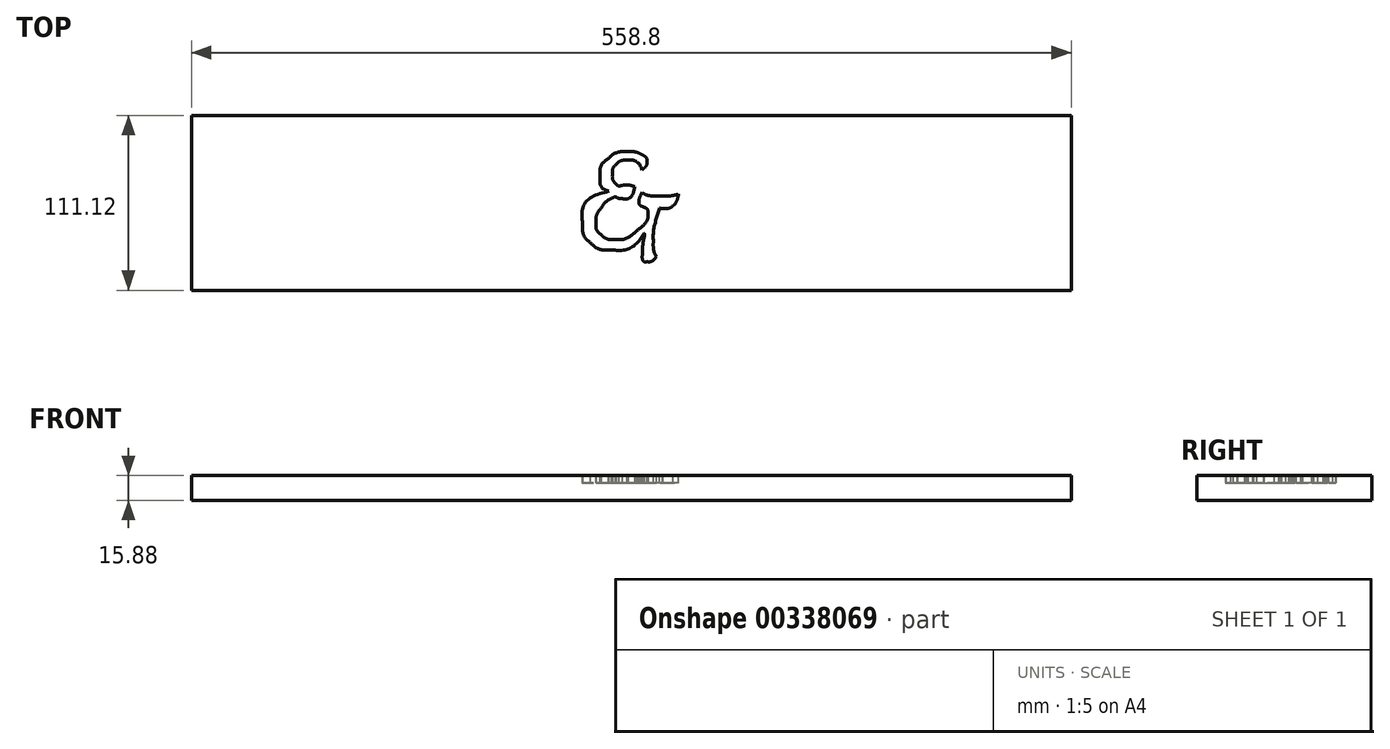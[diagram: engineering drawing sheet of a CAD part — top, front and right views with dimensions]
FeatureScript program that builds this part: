
annotation { "Feature Type Name" : "Feature", "Feature Type Description" : "" }
export const myFeature = defineFeature(function(context is Context, id is Id, definition is map)
    precondition{}
    {
        {
            var Q0;
            Q0=qCreatedBy(makeId("Top.planeOp"),FACE);
            var sketch = newSketch(context, id + "F0", { "sketchPlane" : qUnion([Q0])});
            skLineSegment(sketch, "E0.bottom", {"start": v(12.7, 0) * mm, "end": v(546.1, 0) * mm});
            skLineSegment(sketch, "E0.top", {"start": v(12.7, 609.6) * mm, "end": v(546.1, 609.6) * mm});
            skLineSegment(sketch, "E0.left", {"start": v(0, 12.7) * mm, "end": v(0, 596.9) * mm});
            skLineSegment(sketch, "E0.right", {"start": v(558.8, 12.7) * mm, "end": v(558.8, 596.9) * mm});
            skPoint(sketch, "E1.visualSharp", {"position": v(0, 609.6) * mm});
            skArc(sketch, "E1.filletArc", {"start": v(12.7, 609.6) * mm, "mid": v(3.72, 605.88) * mm, "end": v(0, 596.9) * mm});
            skPoint(sketch, "E2.visualSharp", {"position": v(0, 0) * mm});
            skArc(sketch, "E2.filletArc", {"start": v(0, 12.7) * mm, "mid": v(3.72, 3.72) * mm, "end": v(12.7, 0) * mm});
            skPoint(sketch, "E3.visualSharp", {"position": v(558.8, 0) * mm});
            skArc(sketch, "E3.filletArc", {"start": v(546.1, 0) * mm, "mid": v(555.08, 3.72) * mm, "end": v(558.8, 12.7) * mm});
            skPoint(sketch, "E4.visualSharp", {"position": v(558.8, 609.6) * mm});
            skArc(sketch, "E4.filletArc", {"start": v(558.8, 596.9) * mm, "mid": v(555.08, 605.88) * mm, "end": v(546.1, 609.6) * mm});
            skSolve(sketch);
        }
        {
            var Q0;
            Q0=makeQuery(id+"F0.imprint","IMPRINT",FACE,{"disambiguationData":[TD([[makeQuery(id+"F0.imprint","IMPRINT",EDGE,{"derivedFrom":sQuery(id+"F0.wireOp",EDGE,"E0.bottom")}),1.0]])]});
            extrude(context, id + "F1", {"entities" : qUnion([Q0]), "depth" : 15.88 * mm});
        }
        {
            var Q0;
            Q0=makeQuery(id+"F1.opExtrude","CAP_FACE",FACE,{"disambiguationData":[OSD([sQuery(id+"F0.wireOp",EDGE,"E0.bottom"),sQuery(id+"F0.wireOp",EDGE,"E0.top"),sQuery(id+"F0.wireOp",EDGE,"E0.left"),sQuery(id+"F0.wireOp",EDGE,"E0.right"),sQuery(id+"F0.wireOp",EDGE,"E1.filletArc"),sQuery(id+"F0.wireOp",EDGE,"E2.filletArc"),sQuery(id+"F0.wireOp",EDGE,"E3.filletArc"),sQuery(id+"F0.wireOp",EDGE,"E4.filletArc")])],"isStart":false});
            var sketch = newSketch(context, id + "F2", { "sketchPlane" : qUnion([Q0])});
            skFitSpline(sketch, "E5", {"points": [v(247.46, 485.02) * mm, v(244.22, 485.02) * mm, v(241.38, 482.73) * mm, v(238.94, 478.15) * mm]});
            skFitSpline(sketch, "E6", {"points": [v(238.94, 478.15) * mm, v(236.48, 473.56) * mm, v(235.26, 468.05) * mm, v(235.26, 461.6) * mm]});
            skFitSpline(sketch, "E7", {"points": [v(235.26, 461.6) * mm, v(235.26, 456.87) * mm, v(236.54, 454.5) * mm, v(239.12, 454.5) * mm]});
            skFitSpline(sketch, "E8", {"points": [v(239.12, 454.5) * mm, v(242.2, 454.5) * mm, v(248.34, 462.57) * mm, v(257.6, 478.7) * mm]});
            skFitSpline(sketch, "E9", {"points": [v(257.6, 478.7) * mm, v(257.73, 478.94) * mm, v(258.18, 479.46) * mm, v(258.91, 480.26) * mm]});
            skFitSpline(sketch, "E10", {"points": [v(258.91, 480.26) * mm, v(254.36, 483.44) * mm, v(250.54, 485.02) * mm, v(247.46, 485.02) * mm]});
            skFitSpline(sketch, "E11", {"points": [v(371.38, 485.98) * mm, v(368.47, 485.98) * mm, v(365.74, 484.16) * mm, v(363.18, 480.52) * mm]});
            skFitSpline(sketch, "E12", {"points": [v(363.18, 480.52) * mm, v(360.62, 476.88) * mm, v(359.03, 472.72) * mm, v(358.4, 468.06) * mm]});
            skFitSpline(sketch, "E13", {"points": [v(358.4, 468.06) * mm, v(362.59, 468.32) * mm, v(366.35, 469.82) * mm, v(369.66, 472.53) * mm]});
            skFitSpline(sketch, "E14", {"points": [v(369.66, 472.53) * mm, v(372.98, 475.24) * mm, v(374.64, 478.32) * mm, v(374.64, 481.78) * mm]});
            skFitSpline(sketch, "E15", {"points": [v(374.64, 481.78) * mm, v(374.64, 484.58) * mm, v(373.55, 485.98) * mm, v(371.38, 485.98) * mm]});
            skFitSpline(sketch, "E16", {"points": [v(372.25, 491.45) * mm, v(375.43, 491.45) * mm, v(378, 490.53) * mm, v(379.95, 488.68) * mm]});
            skFitSpline(sketch, "E17", {"points": [v(379.95, 488.68) * mm, v(381.9, 486.84) * mm, v(382.89, 484.38) * mm, v(382.89, 481.3) * mm]});
            skFitSpline(sketch, "E18", {"points": [v(382.89, 481.3) * mm, v(382.89, 476.36) * mm, v(380.3, 472.02) * mm, v(375.12, 468.3) * mm]});
            skFitSpline(sketch, "E19", {"points": [v(375.12, 468.3) * mm, v(369.94, 464.57) * mm, v(364.27, 462.7) * mm, v(358.12, 462.7) * mm]});
            skFitSpline(sketch, "E20", {"points": [v(358.12, 462.7) * mm, v(358.12, 456.15) * mm, v(360.76, 452.87) * mm, v(366.01, 452.87) * mm]});
            skFitSpline(sketch, "E21", {"points": [v(366.01, 452.87) * mm, v(370.84, 452.87) * mm, v(376.2, 455.49) * mm, v(382.13, 460.74) * mm]});
            skFitSpline(sketch, "E22", {"points": [v(382.13, 460.74) * mm, v(388.04, 465.98) * mm, v(393.52, 473.06) * mm, v(398.54, 481.95) * mm]});
            skFitSpline(sketch, "E23", {"points": [v(402.5, 479.62) * mm, v(397.84, 469.55) * mm, v(391.82, 461.33) * mm, v(384.42, 454.98) * mm]});
            skFitSpline(sketch, "E24", {"points": [v(384.42, 454.98) * mm, v(377.03, 448.62) * mm, v(369.98, 445.45) * mm, v(363.3, 445.45) * mm]});
            skFitSpline(sketch, "E25", {"points": [v(363.3, 445.45) * mm, v(358.9, 445.45) * mm, v(355.42, 447.05) * mm, v(352.87, 450.22) * mm]});
            skFitSpline(sketch, "E26", {"points": [v(352.87, 450.22) * mm, v(350.64, 453) * mm, v(349.4, 456.61) * mm, v(349.1, 461.08) * mm]});
            skFitSpline(sketch, "E27", {"points": [v(349.1, 461.08) * mm, v(347.32, 458.56) * mm, v(345.51, 456.33) * mm, v(343.7, 454.35) * mm]});
            skFitSpline(sketch, "E28", {"points": [v(343.7, 454.35) * mm, v(338.24, 448.42) * mm, v(333.27, 445.45) * mm, v(328.8, 445.45) * mm]});
            skFitSpline(sketch, "E29", {"points": [v(328.8, 445.45) * mm, v(325.99, 445.45) * mm, v(323.71, 446.48) * mm, v(322, 448.54) * mm]});
            skFitSpline(sketch, "E30", {"points": [v(322, 448.54) * mm, v(320.27, 450.6) * mm, v(319.41, 453.3) * mm, v(319.41, 456.62) * mm]});
            skFitSpline(sketch, "E31", {"points": [v(319.41, 456.62) * mm, v(319.41, 457.85) * mm, v(319.64, 459.77) * mm, v(320.12, 462.36) * mm]});
            skLineSegment(sketch, "E32", {"start": v(398.54, 481.95) * mm, "end": v(402.5, 479.62) * mm});
            skLineSegment(sketch, "E33", {"start": v(402.5, 479.62) * mm, "end": v(398.54, 481.95) * mm});
            skFitSpline(sketch, "E34", {"points": [v(320.89, 466.68) * mm, v(322, 472.85) * mm, v(322.57, 477.15) * mm, v(322.57, 479.6) * mm]});
            skFitSpline(sketch, "E35", {"points": [v(322.57, 479.6) * mm, v(322.57, 480.87) * mm, v(322.18, 482.24) * mm, v(321.4, 483.7) * mm]});
            skFitSpline(sketch, "E36", {"points": [v(321.4, 483.7) * mm, v(324.84, 484.7) * mm, v(326.97, 485.22) * mm, v(327.78, 485.22) * mm]});
            skFitSpline(sketch, "E37", {"points": [v(327.78, 485.22) * mm, v(329.99, 485.22) * mm, v(331.1, 483.6) * mm, v(331.1, 480.35) * mm]});
            skFitSpline(sketch, "E38", {"points": [v(331.1, 480.35) * mm, v(331.1, 478.32) * mm, v(330.76, 475.38) * mm, v(330.07, 471.54) * mm]});
            skLineSegment(sketch, "E39", {"start": v(320.12, 462.36) * mm, "end": v(320.89, 466.68) * mm});
            skLineSegment(sketch, "E40", {"start": v(320.89, 466.68) * mm, "end": v(320.12, 462.36) * mm});
            skFitSpline(sketch, "E41", {"points": [v(328.7, 463.92) * mm, v(328.05, 460.32) * mm, v(327.73, 458) * mm, v(327.73, 456.92) * mm]});
            skFitSpline(sketch, "E42", {"points": [v(327.73, 456.92) * mm, v(327.73, 454.22) * mm, v(328.7, 452.87) * mm, v(330.64, 452.87) * mm]});
            skFitSpline(sketch, "E43", {"points": [v(330.64, 452.87) * mm, v(333.34, 452.87) * mm, v(337.06, 455.56) * mm, v(341.8, 460.93) * mm]});
            skFitSpline(sketch, "E44", {"points": [v(341.8, 460.93) * mm, v(344.6, 464.12) * mm, v(347.4, 467.87) * mm, v(350.2, 472.2) * mm]});
            skFitSpline(sketch, "E45", {"points": [v(350.2, 472.2) * mm, v(351.28, 476.24) * mm, v(353.16, 479.88) * mm, v(355.83, 483.14) * mm]});
            skFitSpline(sketch, "E46", {"points": [v(355.83, 483.14) * mm, v(360.35, 488.68) * mm, v(365.83, 491.45) * mm, v(372.25, 491.45) * mm]});
            skLineSegment(sketch, "E47", {"start": v(330.07, 471.54) * mm, "end": v(328.7, 463.92) * mm});
            skLineSegment(sketch, "E48", {"start": v(328.7, 463.92) * mm, "end": v(330.07, 471.54) * mm});
            skFitSpline(sketch, "E49", {"points": [v(305.1, 507.84) * mm, v(305.33, 507.84) * mm, v(306.14, 507.78) * mm, v(307.5, 507.65) * mm]});
            skFitSpline(sketch, "E50", {"points": [v(307.5, 507.65) * mm, v(305.64, 504.33) * mm, v(303.76, 499.96) * mm, v(301.86, 494.56) * mm]});
            skFitSpline(sketch, "E51", {"points": [v(319.5, 494.56) * mm, v(322.22, 494.56) * mm, v(324.64, 494.92) * mm, v(326.74, 495.67) * mm]});
            skFitSpline(sketch, "E52", {"points": [v(326.74, 495.67) * mm, v(326.87, 497.05) * mm, v(327.2, 498.41) * mm, v(327.69, 499.77) * mm]});
            skLineSegment(sketch, "E53", {"start": v(301.86, 494.56) * mm, "end": v(319.5, 494.56) * mm});
            skLineSegment(sketch, "E54", {"start": v(319.5, 494.56) * mm, "end": v(301.86, 494.56) * mm});
            skFitSpline(sketch, "E55", {"points": [v(328.67, 499.72) * mm, v(330.08, 499.79) * mm, v(332.2, 500.64) * mm, v(335.04, 502.28) * mm]});
            skFitSpline(sketch, "E56", {"points": [v(335.04, 502.28) * mm, v(337.9, 503.93) * mm, v(340.52, 505.68) * mm, v(342.94, 507.52) * mm]});
            skFitSpline(sketch, "E57", {"points": [v(342.94, 507.52) * mm, v(341.85, 503.08) * mm, v(340.03, 500.06) * mm, v(337.5, 498.48) * mm]});
            skFitSpline(sketch, "E58", {"points": [v(337.5, 498.48) * mm, v(333.26, 493.7) * mm, v(330.34, 491.32) * mm, v(328.76, 491.32) * mm]});
            skFitSpline(sketch, "E59", {"points": [v(328.76, 491.32) * mm, v(327.76, 491.32) * mm, v(327.1, 491.79) * mm, v(326.85, 492.72) * mm]});
            skFitSpline(sketch, "E60", {"points": [v(326.85, 492.72) * mm, v(326.33, 491.05) * mm, v(325.73, 489.92) * mm, v(325.02, 489.33) * mm]});
            skFitSpline(sketch, "E61", {"points": [v(325.02, 489.33) * mm, v(323.92, 488.4) * mm, v(321.98, 487.93) * mm, v(319.18, 487.93) * mm]});
            skLineSegment(sketch, "E62", {"start": v(327.69, 499.77) * mm, "end": v(328.67, 499.72) * mm});
            skLineSegment(sketch, "E63", {"start": v(328.67, 499.72) * mm, "end": v(327.69, 499.77) * mm});
            skFitSpline(sketch, "E64", {"points": [v(300.17, 487.93) * mm, v(300.04, 487.44) * mm, v(299.9, 486.92) * mm, v(299.75, 486.38) * mm]});
            skFitSpline(sketch, "E65", {"points": [v(299.75, 486.38) * mm, v(296.99, 475.84) * mm, v(295.6, 467.88) * mm, v(295.6, 462.47) * mm]});
            skFitSpline(sketch, "E66", {"points": [v(295.6, 462.47) * mm, v(295.6, 456.94) * mm, v(297.3, 454.18) * mm, v(300.68, 454.18) * mm]});
            skFitSpline(sketch, "E67", {"points": [v(300.68, 454.18) * mm, v(302.53, 454.18) * mm, v(304.57, 455.1) * mm, v(306.8, 456.9) * mm]});
            skFitSpline(sketch, "E68", {"points": [v(306.8, 456.9) * mm, v(309.05, 458.71) * mm, v(310.85, 460.91) * mm, v(312.2, 463.5) * mm]});
            skFitSpline(sketch, "E69", {"points": [v(312.2, 463.5) * mm, v(313.35, 461.8) * mm, v(313.92, 460.42) * mm, v(313.92, 459.33) * mm]});
            skFitSpline(sketch, "E70", {"points": [v(313.92, 459.33) * mm, v(313.92, 456.5) * mm, v(311.92, 453.5) * mm, v(307.92, 450.28) * mm]});
            skFitSpline(sketch, "E71", {"points": [v(307.92, 450.28) * mm, v(303.9, 447.06) * mm, v(300.24, 445.45) * mm, v(296.9, 445.45) * mm]});
            skFitSpline(sketch, "E72", {"points": [v(296.9, 445.45) * mm, v(293.88, 445.45) * mm, v(291.42, 446.93) * mm, v(289.56, 449.9) * mm]});
            skFitSpline(sketch, "E73", {"points": [v(289.56, 449.9) * mm, v(287.7, 452.87) * mm, v(286.76, 456.65) * mm, v(286.76, 461.23) * mm]});
            skFitSpline(sketch, "E74", {"points": [v(286.76, 461.23) * mm, v(286.76, 462.58) * mm, v(286.84, 464.08) * mm, v(287.02, 465.75) * mm]});
            skFitSpline(sketch, "E75", {"points": [v(287.02, 465.75) * mm, v(284.81, 462.56) * mm, v(282.47, 459.69) * mm, v(280.01, 457.13) * mm]});
            skFitSpline(sketch, "E76", {"points": [v(280.01, 457.13) * mm, v(274.37, 451.28) * mm, v(269.48, 448.36) * mm, v(265.31, 448.36) * mm]});
            skFitSpline(sketch, "E77", {"points": [v(265.31, 448.36) * mm, v(259.81, 448.36) * mm, v(257.07, 453.3) * mm, v(257.07, 463.23) * mm]});
            skFitSpline(sketch, "E78", {"points": [v(257.07, 463.23) * mm, v(257.07, 465.2) * mm, v(257.14, 467.57) * mm, v(257.28, 470.32) * mm]});
            skFitSpline(sketch, "E79", {"points": [v(257.28, 470.32) * mm, v(255.19, 463.64) * mm, v(251.91, 457.83) * mm, v(247.46, 452.87) * mm]});
            skFitSpline(sketch, "E80", {"points": [v(247.46, 452.87) * mm, v(242.99, 447.92) * mm, v(239.04, 445.45) * mm, v(235.6, 445.45) * mm]});
            skFitSpline(sketch, "E81", {"points": [v(235.6, 445.45) * mm, v(232.88, 445.45) * mm, v(230.72, 446.77) * mm, v(229.15, 449.4) * mm]});
            skFitSpline(sketch, "E82", {"points": [v(229.15, 449.4) * mm, v(227.56, 452.05) * mm, v(226.77, 455.51) * mm, v(226.77, 459.78) * mm]});
            skFitSpline(sketch, "E83", {"points": [v(226.77, 459.78) * mm, v(226.77, 468.13) * mm, v(229.03, 475.5) * mm, v(233.56, 481.87) * mm]});
            skFitSpline(sketch, "E84", {"points": [v(233.56, 481.87) * mm, v(238.09, 488.26) * mm, v(243.35, 491.45) * mm, v(249.38, 491.45) * mm]});
            skFitSpline(sketch, "E85", {"points": [v(249.38, 491.45) * mm, v(253.01, 491.45) * mm, v(256.66, 490.21) * mm, v(260.33, 487.76) * mm]});
            skFitSpline(sketch, "E86", {"points": [v(260.33, 487.76) * mm, v(260.86, 490.19) * mm, v(263.48, 491.4) * mm, v(268.16, 491.4) * mm]});
            skFitSpline(sketch, "E87", {"points": [v(268.16, 491.4) * mm, v(268.26, 491.4) * mm, v(268.96, 491.37) * mm, v(270.27, 491.3) * mm]});
            skFitSpline(sketch, "E88", {"points": [v(270.27, 491.3) * mm, v(268.9, 488.33) * mm, v(267.89, 484.93) * mm, v(267.2, 481.1) * mm]});
            skLineSegment(sketch, "E89", {"start": v(319.18, 487.93) * mm, "end": v(300.17, 487.93) * mm});
            skLineSegment(sketch, "E90", {"start": v(300.17, 487.93) * mm, "end": v(319.18, 487.93) * mm});
            skFitSpline(sketch, "E91", {"points": [v(266.62, 477.77) * mm, v(265.96, 474.15) * mm, v(265.63, 469.88) * mm, v(265.63, 464.94) * mm]});
            skFitSpline(sketch, "E92", {"points": [v(265.63, 464.94) * mm, v(265.63, 459.77) * mm, v(266.57, 457.18) * mm, v(268.44, 457.18) * mm]});
            skFitSpline(sketch, "E93", {"points": [v(268.44, 457.18) * mm, v(270.76, 457.18) * mm, v(274.05, 459.48) * mm, v(278.32, 464.1) * mm]});
            skFitSpline(sketch, "E94", {"points": [v(278.32, 464.1) * mm, v(281.96, 468.04) * mm, v(285.66, 473) * mm, v(289.42, 478.98) * mm]});
            skFitSpline(sketch, "E95", {"points": [v(289.42, 478.98) * mm, v(289.7, 480.18) * mm, v(290, 481.4) * mm, v(290.32, 482.69) * mm]});
            skLineSegment(sketch, "E96", {"start": v(267.2, 481.1) * mm, "end": v(266.62, 477.77) * mm});
            skLineSegment(sketch, "E97", {"start": v(266.62, 477.77) * mm, "end": v(267.2, 481.1) * mm});
            skFitSpline(sketch, "E98", {"points": [v(286.65, 487.93) * mm, v(284.3, 487.93) * mm, v(282.1, 487.54) * mm, v(280.04, 486.76) * mm]});
            skFitSpline(sketch, "E99", {"points": [v(280.04, 486.76) * mm, v(281.5, 490.38) * mm, v(282.72, 492.6) * mm, v(283.72, 493.38) * mm]});
            skFitSpline(sketch, "E100", {"points": [v(283.72, 493.38) * mm, v(284.71, 494.16) * mm, v(286.34, 494.56) * mm, v(288.6, 494.56) * mm]});
            skLineSegment(sketch, "E101", {"start": v(290.32, 482.69) * mm, "end": v(291.82, 487.93) * mm});
            skLineSegment(sketch, "E102", {"start": v(291.82, 487.93) * mm, "end": v(286.65, 487.93) * mm});
            skFitSpline(sketch, "E103", {"points": [v(293.99, 497.12) * mm, v(295.02, 501) * mm, v(296.33, 503.76) * mm, v(297.95, 505.4) * mm]});
            skFitSpline(sketch, "E104", {"points": [v(297.95, 505.4) * mm, v(299.55, 507.03) * mm, v(301.94, 507.84) * mm, v(305.1, 507.84) * mm]});
            skLineSegment(sketch, "E105", {"start": v(288.6, 494.56) * mm, "end": v(293.33, 494.56) * mm});
            skLineSegment(sketch, "E106", {"start": v(293.33, 494.56) * mm, "end": v(293.99, 497.12) * mm});
            skFitSpline(sketch, "E107", {"points": [v(178.41, 506.2) * mm, v(181.96, 506.2) * mm, v(186.85, 506.6) * mm, v(193.08, 507.4) * mm]});
            skFitSpline(sketch, "E108", {"points": [v(188.04, 478.85) * mm, v(200.42, 488.81) * mm, v(207.85, 498.44) * mm, v(210.33, 507.7) * mm]});
            skFitSpline(sketch, "E109", {"points": [v(210.33, 507.7) * mm, v(214.42, 505.56) * mm, v(216.46, 503.26) * mm, v(216.46, 500.79) * mm]});
            skFitSpline(sketch, "E110", {"points": [v(216.46, 500.79) * mm, v(216.46, 499.37) * mm, v(213.98, 496.13) * mm, v(209, 491.1) * mm]});
            skFitSpline(sketch, "E111", {"points": [v(209, 491.1) * mm, v(204.02, 486.08) * mm, v(199.1, 481.73) * mm, v(194.23, 478.07) * mm]});
            skFitSpline(sketch, "E112", {"points": [v(194.23, 478.07) * mm, v(198.39, 469.54) * mm, v(202.46, 462.52) * mm, v(206.43, 457.03) * mm]});
            skFitSpline(sketch, "E113", {"points": [v(206.43, 457.03) * mm, v(210.4, 451.54) * mm, v(213.38, 448.8) * mm, v(215.37, 448.8) * mm]});
            skFitSpline(sketch, "E114", {"points": [v(215.37, 448.8) * mm, v(217.55, 448.8) * mm, v(220.39, 450.27) * mm, v(223.87, 453.22) * mm]});
            skLineSegment(sketch, "E115", {"start": v(193.08, 507.4) * mm, "end": v(188.04, 478.85) * mm});
            skLineSegment(sketch, "E116", {"start": v(188.04, 478.85) * mm, "end": v(193.08, 507.4) * mm});
            skFitSpline(sketch, "E117", {"points": [v(223.98, 451.1) * mm, v(223.98, 449.09) * mm, v(222.68, 446.98) * mm, v(220.08, 444.73) * mm]});
            skFitSpline(sketch, "E118", {"points": [v(220.08, 444.73) * mm, v(217.49, 442.5) * mm, v(214.96, 441.38) * mm, v(212.51, 441.38) * mm]});
            skFitSpline(sketch, "E119", {"points": [v(212.51, 441.38) * mm, v(206.3, 441.38) * mm, v(197.85, 452.5) * mm, v(187.18, 474.76) * mm]});
            skLineSegment(sketch, "E120", {"start": v(223.87, 453.22) * mm, "end": v(223.98, 451.1) * mm});
            skLineSegment(sketch, "E121", {"start": v(223.98, 451.1) * mm, "end": v(223.87, 453.22) * mm});
            skFitSpline(sketch, "E122", {"points": [v(183.9, 454.8) * mm, v(183.48, 452.44) * mm, v(183.27, 450.88) * mm, v(183.27, 450.14) * mm]});
            skFitSpline(sketch, "E123", {"points": [v(183.27, 450.14) * mm, v(183.27, 449.5) * mm, v(183.42, 448.6) * mm, v(183.73, 447.42) * mm]});
            skFitSpline(sketch, "E124", {"points": [v(183.73, 447.42) * mm, v(180.96, 445.82) * mm, v(178.55, 445.01) * mm, v(176.52, 445.01) * mm]});
            skFitSpline(sketch, "E125", {"points": [v(176.52, 445.01) * mm, v(174.84, 445.01) * mm, v(174, 445.83) * mm, v(174, 447.45) * mm]});
            skFitSpline(sketch, "E126", {"points": [v(174, 447.45) * mm, v(174, 448.08) * mm, v(174.25, 449.8) * mm, v(174.74, 452.56) * mm]});
            skLineSegment(sketch, "E127", {"start": v(187.18, 474.76) * mm, "end": v(183.9, 454.8) * mm});
            skLineSegment(sketch, "E128", {"start": v(183.9, 454.8) * mm, "end": v(187.18, 474.76) * mm});
            skFitSpline(sketch, "E129", {"points": [v(183.17, 499.25) * mm, v(181.66, 498.94) * mm, v(180, 498.79) * mm, v(178.17, 498.79) * mm]});
            skFitSpline(sketch, "E130", {"points": [v(178.17, 498.79) * mm, v(174.1, 498.79) * mm, v(171.7, 502.02) * mm, v(170.94, 508.51) * mm]});
            skLineSegment(sketch, "E131", {"start": v(174.74, 452.56) * mm, "end": v(183.17, 499.25) * mm});
            skLineSegment(sketch, "E132", {"start": v(183.17, 499.25) * mm, "end": v(174.74, 452.56) * mm});
            skFitSpline(sketch, "E133", {"points": [v(247.46, 485.02) * mm, v(244.22, 485.02) * mm, v(241.38, 482.73) * mm, v(238.94, 478.15) * mm]});
            skFitSpline(sketch, "E134", {"points": [v(238.94, 478.15) * mm, v(236.48, 473.56) * mm, v(235.26, 468.05) * mm, v(235.26, 461.6) * mm]});
            skFitSpline(sketch, "E135", {"points": [v(235.26, 461.6) * mm, v(235.26, 456.87) * mm, v(236.54, 454.5) * mm, v(239.12, 454.5) * mm]});
            skFitSpline(sketch, "E136", {"points": [v(239.12, 454.5) * mm, v(242.2, 454.5) * mm, v(248.34, 462.57) * mm, v(257.6, 478.7) * mm]});
            skFitSpline(sketch, "E137", {"points": [v(257.6, 478.7) * mm, v(257.73, 478.94) * mm, v(258.18, 479.46) * mm, v(258.91, 480.26) * mm]});
            skFitSpline(sketch, "E138", {"points": [v(258.91, 480.26) * mm, v(254.36, 483.44) * mm, v(250.54, 485.02) * mm, v(247.46, 485.02) * mm]});
            skFitSpline(sketch, "E139", {"points": [v(371.38, 485.98) * mm, v(368.47, 485.98) * mm, v(365.74, 484.16) * mm, v(363.18, 480.52) * mm]});
            skFitSpline(sketch, "E140", {"points": [v(363.18, 480.52) * mm, v(360.62, 476.88) * mm, v(359.03, 472.72) * mm, v(358.4, 468.06) * mm]});
            skFitSpline(sketch, "E141", {"points": [v(358.4, 468.06) * mm, v(362.59, 468.32) * mm, v(366.35, 469.82) * mm, v(369.66, 472.53) * mm]});
            skFitSpline(sketch, "E142", {"points": [v(369.66, 472.53) * mm, v(372.98, 475.24) * mm, v(374.64, 478.32) * mm, v(374.64, 481.78) * mm]});
            skFitSpline(sketch, "E143", {"points": [v(374.64, 481.78) * mm, v(374.64, 484.58) * mm, v(373.55, 485.98) * mm, v(371.38, 485.98) * mm]});
            skFitSpline(sketch, "E144", {"points": [v(372.25, 491.45) * mm, v(375.43, 491.45) * mm, v(378, 490.53) * mm, v(379.95, 488.68) * mm]});
            skFitSpline(sketch, "E145", {"points": [v(379.95, 488.68) * mm, v(381.9, 486.84) * mm, v(382.89, 484.38) * mm, v(382.89, 481.3) * mm]});
            skFitSpline(sketch, "E146", {"points": [v(382.89, 481.3) * mm, v(382.89, 476.36) * mm, v(380.3, 472.02) * mm, v(375.12, 468.3) * mm]});
            skFitSpline(sketch, "E147", {"points": [v(375.12, 468.3) * mm, v(369.94, 464.57) * mm, v(364.27, 462.7) * mm, v(358.12, 462.7) * mm]});
            skFitSpline(sketch, "E148", {"points": [v(358.12, 462.7) * mm, v(358.12, 456.15) * mm, v(360.76, 452.87) * mm, v(366.01, 452.87) * mm]});
            skFitSpline(sketch, "E149", {"points": [v(366.01, 452.87) * mm, v(370.84, 452.87) * mm, v(376.2, 455.49) * mm, v(382.13, 460.74) * mm]});
            skFitSpline(sketch, "E150", {"points": [v(382.13, 460.74) * mm, v(388.04, 465.98) * mm, v(393.52, 473.06) * mm, v(398.54, 481.95) * mm]});
            skFitSpline(sketch, "E151", {"points": [v(402.5, 479.62) * mm, v(397.84, 469.55) * mm, v(391.82, 461.33) * mm, v(384.42, 454.98) * mm]});
            skFitSpline(sketch, "E152", {"points": [v(384.42, 454.98) * mm, v(377.03, 448.62) * mm, v(369.98, 445.45) * mm, v(363.3, 445.45) * mm]});
            skFitSpline(sketch, "E153", {"points": [v(363.3, 445.45) * mm, v(358.9, 445.45) * mm, v(355.42, 447.05) * mm, v(352.87, 450.22) * mm]});
            skFitSpline(sketch, "E154", {"points": [v(352.87, 450.22) * mm, v(350.64, 453) * mm, v(349.4, 456.61) * mm, v(349.1, 461.08) * mm]});
            skFitSpline(sketch, "E155", {"points": [v(349.1, 461.08) * mm, v(347.32, 458.56) * mm, v(345.51, 456.33) * mm, v(343.7, 454.35) * mm]});
            skFitSpline(sketch, "E156", {"points": [v(343.7, 454.35) * mm, v(338.24, 448.42) * mm, v(333.27, 445.45) * mm, v(328.8, 445.45) * mm]});
            skFitSpline(sketch, "E157", {"points": [v(328.8, 445.45) * mm, v(325.99, 445.45) * mm, v(323.71, 446.48) * mm, v(322, 448.54) * mm]});
            skFitSpline(sketch, "E158", {"points": [v(322, 448.54) * mm, v(320.27, 450.6) * mm, v(319.41, 453.3) * mm, v(319.41, 456.62) * mm]});
            skFitSpline(sketch, "E159", {"points": [v(319.41, 456.62) * mm, v(319.41, 457.85) * mm, v(319.64, 459.77) * mm, v(320.12, 462.36) * mm]});
            skFitSpline(sketch, "E160", {"points": [v(320.89, 466.68) * mm, v(322, 472.85) * mm, v(322.57, 477.15) * mm, v(322.57, 479.6) * mm]});
            skFitSpline(sketch, "E161", {"points": [v(322.57, 479.6) * mm, v(322.57, 480.87) * mm, v(322.18, 482.24) * mm, v(321.4, 483.7) * mm]});
            skFitSpline(sketch, "E162", {"points": [v(321.4, 483.7) * mm, v(324.84, 484.7) * mm, v(326.97, 485.22) * mm, v(327.78, 485.22) * mm]});
            skFitSpline(sketch, "E163", {"points": [v(327.78, 485.22) * mm, v(329.99, 485.22) * mm, v(331.1, 483.6) * mm, v(331.1, 480.35) * mm]});
            skFitSpline(sketch, "E164", {"points": [v(331.1, 480.35) * mm, v(331.1, 478.32) * mm, v(330.76, 475.38) * mm, v(330.07, 471.54) * mm]});
            skFitSpline(sketch, "E165", {"points": [v(328.7, 463.92) * mm, v(328.05, 460.32) * mm, v(327.73, 458) * mm, v(327.73, 456.92) * mm]});
            skFitSpline(sketch, "E166", {"points": [v(327.73, 456.92) * mm, v(327.73, 454.22) * mm, v(328.7, 452.87) * mm, v(330.64, 452.87) * mm]});
            skFitSpline(sketch, "E167", {"points": [v(330.64, 452.87) * mm, v(333.34, 452.87) * mm, v(337.06, 455.56) * mm, v(341.8, 460.93) * mm]});
            skFitSpline(sketch, "E168", {"points": [v(341.8, 460.93) * mm, v(344.6, 464.12) * mm, v(347.4, 467.87) * mm, v(350.2, 472.2) * mm]});
            skFitSpline(sketch, "E169", {"points": [v(350.2, 472.2) * mm, v(351.28, 476.24) * mm, v(353.16, 479.88) * mm, v(355.83, 483.14) * mm]});
            skFitSpline(sketch, "E170", {"points": [v(355.83, 483.14) * mm, v(360.35, 488.68) * mm, v(365.83, 491.45) * mm, v(372.25, 491.45) * mm]});
            skFitSpline(sketch, "E171", {"points": [v(305.1, 507.84) * mm, v(305.33, 507.84) * mm, v(306.14, 507.78) * mm, v(307.5, 507.65) * mm]});
            skFitSpline(sketch, "E172", {"points": [v(307.5, 507.65) * mm, v(305.64, 504.33) * mm, v(303.76, 499.96) * mm, v(301.86, 494.56) * mm]});
            skFitSpline(sketch, "E173", {"points": [v(319.5, 494.56) * mm, v(322.22, 494.56) * mm, v(324.64, 494.92) * mm, v(326.74, 495.67) * mm]});
            skFitSpline(sketch, "E174", {"points": [v(326.74, 495.67) * mm, v(326.87, 497.05) * mm, v(327.2, 498.41) * mm, v(327.69, 499.77) * mm]});
            skFitSpline(sketch, "E175", {"points": [v(328.67, 499.72) * mm, v(330.08, 499.79) * mm, v(332.2, 500.64) * mm, v(335.04, 502.28) * mm]});
            skFitSpline(sketch, "E176", {"points": [v(335.04, 502.28) * mm, v(337.9, 503.93) * mm, v(340.52, 505.68) * mm, v(342.94, 507.52) * mm]});
            skFitSpline(sketch, "E177", {"points": [v(342.94, 507.52) * mm, v(341.85, 503.08) * mm, v(340.03, 500.06) * mm, v(337.5, 498.48) * mm]});
            skFitSpline(sketch, "E178", {"points": [v(337.5, 498.48) * mm, v(333.26, 493.7) * mm, v(330.34, 491.32) * mm, v(328.76, 491.32) * mm]});
            skFitSpline(sketch, "E179", {"points": [v(328.76, 491.32) * mm, v(327.76, 491.32) * mm, v(327.1, 491.79) * mm, v(326.85, 492.72) * mm]});
            skFitSpline(sketch, "E180", {"points": [v(326.85, 492.72) * mm, v(326.33, 491.05) * mm, v(325.73, 489.92) * mm, v(325.02, 489.33) * mm]});
            skFitSpline(sketch, "E181", {"points": [v(325.02, 489.33) * mm, v(323.92, 488.4) * mm, v(321.98, 487.93) * mm, v(319.18, 487.93) * mm]});
            skFitSpline(sketch, "E182", {"points": [v(300.17, 487.93) * mm, v(300.04, 487.44) * mm, v(299.9, 486.92) * mm, v(299.75, 486.38) * mm]});
            skFitSpline(sketch, "E183", {"points": [v(299.75, 486.38) * mm, v(296.99, 475.84) * mm, v(295.6, 467.88) * mm, v(295.6, 462.47) * mm]});
            skFitSpline(sketch, "E184", {"points": [v(295.6, 462.47) * mm, v(295.6, 456.94) * mm, v(297.3, 454.18) * mm, v(300.68, 454.18) * mm]});
            skFitSpline(sketch, "E185", {"points": [v(300.68, 454.18) * mm, v(302.53, 454.18) * mm, v(304.57, 455.1) * mm, v(306.8, 456.9) * mm]});
            skFitSpline(sketch, "E186", {"points": [v(306.8, 456.9) * mm, v(309.05, 458.71) * mm, v(310.85, 460.91) * mm, v(312.2, 463.5) * mm]});
            skFitSpline(sketch, "E187", {"points": [v(312.2, 463.5) * mm, v(313.35, 461.8) * mm, v(313.92, 460.42) * mm, v(313.92, 459.33) * mm]});
            skFitSpline(sketch, "E188", {"points": [v(313.92, 459.33) * mm, v(313.92, 456.5) * mm, v(311.92, 453.5) * mm, v(307.92, 450.28) * mm]});
            skFitSpline(sketch, "E189", {"points": [v(307.92, 450.28) * mm, v(303.9, 447.06) * mm, v(300.24, 445.45) * mm, v(296.9, 445.45) * mm]});
            skFitSpline(sketch, "E190", {"points": [v(296.9, 445.45) * mm, v(293.88, 445.45) * mm, v(291.42, 446.93) * mm, v(289.56, 449.9) * mm]});
            skFitSpline(sketch, "E191", {"points": [v(289.56, 449.9) * mm, v(287.7, 452.87) * mm, v(286.76, 456.65) * mm, v(286.76, 461.23) * mm]});
            skFitSpline(sketch, "E192", {"points": [v(286.76, 461.23) * mm, v(286.76, 462.58) * mm, v(286.84, 464.08) * mm, v(287.02, 465.75) * mm]});
            skFitSpline(sketch, "E193", {"points": [v(287.02, 465.75) * mm, v(284.81, 462.56) * mm, v(282.47, 459.69) * mm, v(280.01, 457.13) * mm]});
            skFitSpline(sketch, "E194", {"points": [v(280.01, 457.13) * mm, v(274.37, 451.28) * mm, v(269.48, 448.36) * mm, v(265.31, 448.36) * mm]});
            skFitSpline(sketch, "E195", {"points": [v(265.31, 448.36) * mm, v(259.81, 448.36) * mm, v(257.07, 453.3) * mm, v(257.07, 463.23) * mm]});
            skFitSpline(sketch, "E196", {"points": [v(257.07, 463.23) * mm, v(257.07, 465.2) * mm, v(257.14, 467.57) * mm, v(257.28, 470.32) * mm]});
            skFitSpline(sketch, "E197", {"points": [v(257.28, 470.32) * mm, v(255.19, 463.64) * mm, v(251.91, 457.83) * mm, v(247.46, 452.87) * mm]});
            skFitSpline(sketch, "E198", {"points": [v(247.46, 452.87) * mm, v(242.99, 447.92) * mm, v(239.04, 445.45) * mm, v(235.6, 445.45) * mm]});
            skFitSpline(sketch, "E199", {"points": [v(235.6, 445.45) * mm, v(232.88, 445.45) * mm, v(230.72, 446.77) * mm, v(229.15, 449.4) * mm]});
            skFitSpline(sketch, "E200", {"points": [v(229.15, 449.4) * mm, v(227.56, 452.05) * mm, v(226.77, 455.51) * mm, v(226.77, 459.78) * mm]});
            skFitSpline(sketch, "E201", {"points": [v(226.77, 459.78) * mm, v(226.77, 468.13) * mm, v(229.03, 475.5) * mm, v(233.56, 481.87) * mm]});
            skFitSpline(sketch, "E202", {"points": [v(233.56, 481.87) * mm, v(238.09, 488.26) * mm, v(243.35, 491.45) * mm, v(249.38, 491.45) * mm]});
            skFitSpline(sketch, "E203", {"points": [v(249.38, 491.45) * mm, v(253.01, 491.45) * mm, v(256.66, 490.21) * mm, v(260.33, 487.76) * mm]});
            skFitSpline(sketch, "E204", {"points": [v(260.33, 487.76) * mm, v(260.86, 490.19) * mm, v(263.48, 491.4) * mm, v(268.16, 491.4) * mm]});
            skFitSpline(sketch, "E205", {"points": [v(268.16, 491.4) * mm, v(268.26, 491.4) * mm, v(268.96, 491.37) * mm, v(270.27, 491.3) * mm]});
            skFitSpline(sketch, "E206", {"points": [v(270.27, 491.3) * mm, v(268.9, 488.33) * mm, v(267.89, 484.93) * mm, v(267.2, 481.1) * mm]});
            skFitSpline(sketch, "E207", {"points": [v(266.62, 477.77) * mm, v(265.96, 474.15) * mm, v(265.63, 469.88) * mm, v(265.63, 464.94) * mm]});
            skFitSpline(sketch, "E208", {"points": [v(265.63, 464.94) * mm, v(265.63, 459.77) * mm, v(266.57, 457.18) * mm, v(268.44, 457.18) * mm]});
            skFitSpline(sketch, "E209", {"points": [v(268.44, 457.18) * mm, v(270.76, 457.18) * mm, v(274.05, 459.48) * mm, v(278.32, 464.1) * mm]});
            skFitSpline(sketch, "E210", {"points": [v(278.32, 464.1) * mm, v(281.96, 468.04) * mm, v(285.66, 473) * mm, v(289.42, 478.98) * mm]});
            skFitSpline(sketch, "E211", {"points": [v(289.42, 478.98) * mm, v(289.7, 480.18) * mm, v(290, 481.4) * mm, v(290.32, 482.69) * mm]});
            skFitSpline(sketch, "E212", {"points": [v(286.65, 487.93) * mm, v(284.3, 487.93) * mm, v(282.1, 487.54) * mm, v(280.04, 486.76) * mm]});
            skFitSpline(sketch, "E213", {"points": [v(280.04, 486.76) * mm, v(281.5, 490.38) * mm, v(282.72, 492.6) * mm, v(283.72, 493.38) * mm]});
            skFitSpline(sketch, "E214", {"points": [v(283.72, 493.38) * mm, v(284.71, 494.16) * mm, v(286.34, 494.56) * mm, v(288.6, 494.56) * mm]});
            skFitSpline(sketch, "E215", {"points": [v(293.99, 497.12) * mm, v(295.02, 501) * mm, v(296.33, 503.76) * mm, v(297.95, 505.4) * mm]});
            skFitSpline(sketch, "E216", {"points": [v(297.95, 505.4) * mm, v(299.55, 507.03) * mm, v(301.94, 507.84) * mm, v(305.1, 507.84) * mm]});
            skFitSpline(sketch, "E217", {"points": [v(170.94, 508.51) * mm, v(173.27, 506.97) * mm, v(175.75, 506.2) * mm, v(178.41, 506.2) * mm]});
            skFitSpline(sketch, "E218", {"points": [v(178.41, 506.2) * mm, v(181.96, 506.2) * mm, v(186.85, 506.6) * mm, v(193.08, 507.4) * mm]});
            skFitSpline(sketch, "E219", {"points": [v(188.04, 478.85) * mm, v(200.42, 488.81) * mm, v(207.85, 498.44) * mm, v(210.33, 507.7) * mm]});
            skFitSpline(sketch, "E220", {"points": [v(210.33, 507.7) * mm, v(214.42, 505.56) * mm, v(216.46, 503.26) * mm, v(216.46, 500.79) * mm]});
            skFitSpline(sketch, "E221", {"points": [v(216.46, 500.79) * mm, v(216.46, 499.37) * mm, v(213.98, 496.13) * mm, v(209, 491.1) * mm]});
            skFitSpline(sketch, "E222", {"points": [v(209, 491.1) * mm, v(204.02, 486.08) * mm, v(199.1, 481.73) * mm, v(194.23, 478.07) * mm]});
            skFitSpline(sketch, "E223", {"points": [v(194.23, 478.07) * mm, v(198.39, 469.54) * mm, v(202.46, 462.52) * mm, v(206.43, 457.03) * mm]});
            skFitSpline(sketch, "E224", {"points": [v(206.43, 457.03) * mm, v(210.4, 451.54) * mm, v(213.38, 448.8) * mm, v(215.37, 448.8) * mm]});
            skFitSpline(sketch, "E225", {"points": [v(215.37, 448.8) * mm, v(217.55, 448.8) * mm, v(220.39, 450.27) * mm, v(223.87, 453.22) * mm]});
            skFitSpline(sketch, "E226", {"points": [v(223.98, 451.1) * mm, v(223.98, 449.09) * mm, v(222.68, 446.98) * mm, v(220.08, 444.73) * mm]});
            skFitSpline(sketch, "E227", {"points": [v(220.08, 444.73) * mm, v(217.49, 442.5) * mm, v(214.96, 441.38) * mm, v(212.51, 441.38) * mm]});
            skFitSpline(sketch, "E228", {"points": [v(212.51, 441.38) * mm, v(206.3, 441.38) * mm, v(197.85, 452.5) * mm, v(187.18, 474.76) * mm]});
            skFitSpline(sketch, "E229", {"points": [v(183.9, 454.8) * mm, v(183.48, 452.44) * mm, v(183.27, 450.88) * mm, v(183.27, 450.14) * mm]});
            skFitSpline(sketch, "E230", {"points": [v(183.27, 450.14) * mm, v(183.27, 449.5) * mm, v(183.42, 448.6) * mm, v(183.73, 447.42) * mm]});
            skFitSpline(sketch, "E231", {"points": [v(183.73, 447.42) * mm, v(180.96, 445.82) * mm, v(178.55, 445.01) * mm, v(176.52, 445.01) * mm]});
            skFitSpline(sketch, "E232", {"points": [v(176.52, 445.01) * mm, v(174.84, 445.01) * mm, v(174, 445.83) * mm, v(174, 447.45) * mm]});
            skFitSpline(sketch, "E233", {"points": [v(174, 447.45) * mm, v(174, 448.08) * mm, v(174.25, 449.8) * mm, v(174.74, 452.56) * mm]});
            skFitSpline(sketch, "E234", {"points": [v(183.17, 499.25) * mm, v(181.66, 498.94) * mm, v(180, 498.79) * mm, v(178.17, 498.79) * mm]});
            skFitSpline(sketch, "E235", {"points": [v(178.17, 498.79) * mm, v(174.1, 498.79) * mm, v(171.7, 502.02) * mm, v(170.94, 508.51) * mm]});
            skFitSpline(sketch, "E236", {"points": [v(277.79, 394.65) * mm, v(280.95, 394.65) * mm, v(283.67, 394.04) * mm, v(285.93, 392.83) * mm]});
            skFitSpline(sketch, "E237", {"points": [v(285.93, 392.83) * mm, v(288.2, 391.61) * mm, v(289.33, 390.05) * mm, v(289.33, 388.1) * mm]});
            skFitSpline(sketch, "E238", {"points": [v(289.33, 388.1) * mm, v(289.33, 386.55) * mm, v(288.3, 384.9) * mm, v(286.28, 383.13) * mm]});
            skFitSpline(sketch, "E239", {"points": [v(286.28, 383.13) * mm, v(284.16, 387.16) * mm, v(281.01, 389.18) * mm, v(276.84, 389.18) * mm]});
            skFitSpline(sketch, "E240", {"points": [v(276.84, 389.18) * mm, v(274.08, 389.18) * mm, v(271.82, 388.38) * mm, v(270.07, 386.75) * mm]});
            skFitSpline(sketch, "E241", {"points": [v(270.07, 386.75) * mm, v(268.32, 385.12) * mm, v(267.44, 383.06) * mm, v(267.44, 380.56) * mm]});
            skFitSpline(sketch, "E242", {"points": [v(267.44, 380.56) * mm, v(267.44, 377.66) * mm, v(268.8, 375.02) * mm, v(271.5, 372.69) * mm]});
            skFitSpline(sketch, "E243", {"points": [v(271.5, 372.69) * mm, v(273.4, 373.18) * mm, v(275.11, 373.43) * mm, v(276.63, 373.43) * mm]});
            skFitSpline(sketch, "E244", {"points": [v(276.63, 373.43) * mm, v(278.07, 373.43) * mm, v(279.73, 373.08) * mm, v(281.63, 372.4) * mm]});
            skFitSpline(sketch, "E245", {"points": [v(281.63, 372.4) * mm, v(280.16, 367.34) * mm, v(277.58, 364.81) * mm, v(273.88, 364.81) * mm]});
            skFitSpline(sketch, "E246", {"points": [v(273.88, 364.81) * mm, v(272.36, 364.81) * mm, v(270.86, 365.22) * mm, v(269.35, 366.02) * mm]});
            skFitSpline(sketch, "E247", {"points": [v(269.35, 366.02) * mm, v(265.7, 364.5) * mm, v(262.72, 362.19) * mm, v(260.42, 359.13) * mm]});
            skFitSpline(sketch, "E248", {"points": [v(260.42, 359.13) * mm, v(258.12, 356.06) * mm, v(256.96, 352.8) * mm, v(256.96, 349.32) * mm]});
            skFitSpline(sketch, "E249", {"points": [v(256.96, 349.32) * mm, v(256.96, 346.25) * mm, v(258.1, 343.74) * mm, v(260.39, 341.8) * mm]});
            skFitSpline(sketch, "E250", {"points": [v(260.39, 341.8) * mm, v(262.67, 339.86) * mm, v(265.66, 338.88) * mm, v(269.4, 338.88) * mm]});
            skFitSpline(sketch, "E251", {"points": [v(269.4, 338.88) * mm, v(273.9, 338.88) * mm, v(278.46, 340.78) * mm, v(283.03, 344.56) * mm]});
            skFitSpline(sketch, "E252", {"points": [v(283.03, 344.56) * mm, v(287.61, 348.33) * mm, v(289.9, 352.03) * mm, v(289.9, 355.63) * mm]});
            skFitSpline(sketch, "E253", {"points": [v(289.9, 355.63) * mm, v(289.9, 357.33) * mm, v(289.16, 358.57) * mm, v(287.7, 359.33) * mm]});
            skFitSpline(sketch, "E254", {"points": [v(286.49, 359.8) * mm, v(285.1, 360.5) * mm, v(284.39, 361.54) * mm, v(284.39, 362.92) * mm]});
            skFitSpline(sketch, "E255", {"points": [v(284.39, 362.92) * mm, v(284.39, 364.24) * mm, v(284.98, 366.15) * mm, v(286.17, 368.6) * mm]});
            skFitSpline(sketch, "E256", {"points": [v(286.17, 368.6) * mm, v(289.42, 367.14) * mm, v(293.87, 366.41) * mm, v(299.52, 366.41) * mm]});
            skFitSpline(sketch, "E257", {"points": [v(299.52, 366.41) * mm, v(302.52, 366.41) * mm, v(305.82, 366.82) * mm, v(309.44, 367.62) * mm]});
            skFitSpline(sketch, "E258", {"points": [v(309.44, 367.62) * mm, v(308.5, 363.93) * mm, v(307.32, 361.5) * mm, v(305.9, 360.33) * mm]});
            skFitSpline(sketch, "E259", {"points": [v(305.9, 360.33) * mm, v(304.46, 359.17) * mm, v(302.3, 358.6) * mm, v(299.4, 358.6) * mm]});
            skFitSpline(sketch, "E260", {"points": [v(299.4, 358.6) * mm, v(298.84, 358.6) * mm, v(298.17, 358.64) * mm, v(297.4, 358.75) * mm]});
            skFitSpline(sketch, "E261", {"points": [v(297.4, 358.75) * mm, v(294.74, 350.17) * mm, v(293.41, 343.18) * mm, v(293.41, 337.77) * mm]});
            skFitSpline(sketch, "E262", {"points": [v(293.41, 337.77) * mm, v(293.41, 333.72) * mm, v(294.08, 330.44) * mm, v(295.4, 327.95) * mm]});
            skFitSpline(sketch, "E263", {"points": [v(295.4, 327.95) * mm, v(293.52, 325.82) * mm, v(291.53, 324.77) * mm, v(289.43, 324.77) * mm]});
            skFitSpline(sketch, "E264", {"points": [v(289.43, 324.77) * mm, v(287.44, 324.77) * mm, v(286.45, 326.37) * mm, v(286.45, 329.58) * mm]});
            skFitSpline(sketch, "E265", {"points": [v(288.26, 343.75) * mm, v(282.52, 336.1) * mm, v(275.37, 332.25) * mm, v(266.85, 332.25) * mm]});
            skFitSpline(sketch, "E266", {"points": [v(266.85, 332.25) * mm, v(261.33, 332.25) * mm, v(256.9, 333.76) * mm, v(253.56, 336.78) * mm]});
            skFitSpline(sketch, "E267", {"points": [v(253.56, 336.78) * mm, v(250.21, 339.8) * mm, v(248.55, 343.84) * mm, v(248.55, 348.92) * mm]});
            skFitSpline(sketch, "E268", {"points": [v(248.55, 348.92) * mm, v(248.55, 358.85) * mm, v(254.08, 365.7) * mm, v(265.16, 369.52) * mm]});
            skFitSpline(sketch, "E269", {"points": [v(265.16, 369.52) * mm, v(261.45, 371.14) * mm, v(259.6, 374.46) * mm, v(259.6, 379.46) * mm]});
            skFitSpline(sketch, "E270", {"points": [v(259.6, 379.46) * mm, v(259.6, 383.85) * mm, v(261.34, 387.47) * mm, v(264.82, 390.34) * mm]});
            skFitSpline(sketch, "E271", {"points": [v(264.82, 390.34) * mm, v(268.3, 393.21) * mm, v(272.62, 394.65) * mm, v(277.79, 394.65) * mm]});
            skLineSegment(sketch, "E272", {"start": v(287.7, 359.33) * mm, "end": v(286.49, 359.8) * mm});
            skLineSegment(sketch, "E273", {"start": v(286.49, 359.8) * mm, "end": v(287.7, 359.33) * mm});
            skFitSpline(sketch, "E274", {"points": [v(277.79, 394.65) * mm, v(280.95, 394.65) * mm, v(283.67, 394.04) * mm, v(285.93, 392.83) * mm]});
            skFitSpline(sketch, "E275", {"points": [v(285.93, 392.83) * mm, v(288.2, 391.61) * mm, v(289.33, 390.05) * mm, v(289.33, 388.1) * mm]});
            skFitSpline(sketch, "E276", {"points": [v(289.33, 388.1) * mm, v(289.33, 386.55) * mm, v(288.3, 384.9) * mm, v(286.28, 383.13) * mm]});
            skFitSpline(sketch, "E277", {"points": [v(286.28, 383.13) * mm, v(284.16, 387.16) * mm, v(281.01, 389.18) * mm, v(276.84, 389.18) * mm]});
            skFitSpline(sketch, "E278", {"points": [v(276.84, 389.18) * mm, v(274.08, 389.18) * mm, v(271.82, 388.38) * mm, v(270.07, 386.75) * mm]});
            skFitSpline(sketch, "E279", {"points": [v(270.07, 386.75) * mm, v(268.32, 385.12) * mm, v(267.44, 383.06) * mm, v(267.44, 380.56) * mm]});
            skFitSpline(sketch, "E280", {"points": [v(267.44, 380.56) * mm, v(267.44, 377.66) * mm, v(268.8, 375.02) * mm, v(271.5, 372.69) * mm]});
            skFitSpline(sketch, "E281", {"points": [v(271.5, 372.69) * mm, v(273.4, 373.18) * mm, v(275.11, 373.43) * mm, v(276.63, 373.43) * mm]});
            skFitSpline(sketch, "E282", {"points": [v(276.63, 373.43) * mm, v(278.07, 373.43) * mm, v(279.73, 373.08) * mm, v(281.63, 372.4) * mm]});
            skFitSpline(sketch, "E283", {"points": [v(281.63, 372.4) * mm, v(280.16, 367.34) * mm, v(277.58, 364.81) * mm, v(273.88, 364.81) * mm]});
            skFitSpline(sketch, "E284", {"points": [v(273.88, 364.81) * mm, v(272.36, 364.81) * mm, v(270.86, 365.22) * mm, v(269.35, 366.02) * mm]});
            skFitSpline(sketch, "E285", {"points": [v(269.35, 366.02) * mm, v(265.7, 364.5) * mm, v(262.72, 362.19) * mm, v(260.42, 359.13) * mm]});
            skFitSpline(sketch, "E286", {"points": [v(260.42, 359.13) * mm, v(258.12, 356.06) * mm, v(256.96, 352.8) * mm, v(256.96, 349.32) * mm]});
            skFitSpline(sketch, "E287", {"points": [v(256.96, 349.32) * mm, v(256.96, 346.25) * mm, v(258.1, 343.74) * mm, v(260.39, 341.8) * mm]});
            skFitSpline(sketch, "E288", {"points": [v(260.39, 341.8) * mm, v(262.67, 339.86) * mm, v(265.66, 338.88) * mm, v(269.4, 338.88) * mm]});
            skFitSpline(sketch, "E289", {"points": [v(269.4, 338.88) * mm, v(273.9, 338.88) * mm, v(278.46, 340.78) * mm, v(283.03, 344.56) * mm]});
            skFitSpline(sketch, "E290", {"points": [v(283.03, 344.56) * mm, v(287.61, 348.33) * mm, v(289.9, 352.03) * mm, v(289.9, 355.63) * mm]});
            skFitSpline(sketch, "E291", {"points": [v(289.9, 355.63) * mm, v(289.9, 357.33) * mm, v(289.16, 358.57) * mm, v(287.7, 359.33) * mm]});
            skFitSpline(sketch, "E292", {"points": [v(286.49, 359.8) * mm, v(285.1, 360.5) * mm, v(284.39, 361.54) * mm, v(284.39, 362.92) * mm]});
            skFitSpline(sketch, "E293", {"points": [v(284.39, 362.92) * mm, v(284.39, 364.24) * mm, v(284.98, 366.15) * mm, v(286.17, 368.6) * mm]});
            skFitSpline(sketch, "E294", {"points": [v(286.17, 368.6) * mm, v(289.42, 367.14) * mm, v(293.87, 366.41) * mm, v(299.52, 366.41) * mm]});
            skFitSpline(sketch, "E295", {"points": [v(299.52, 366.41) * mm, v(302.52, 366.41) * mm, v(305.82, 366.82) * mm, v(309.44, 367.62) * mm]});
            skFitSpline(sketch, "E296", {"points": [v(309.44, 367.62) * mm, v(308.5, 363.93) * mm, v(307.32, 361.5) * mm, v(305.9, 360.33) * mm]});
            skFitSpline(sketch, "E297", {"points": [v(305.9, 360.33) * mm, v(304.46, 359.17) * mm, v(302.3, 358.6) * mm, v(299.4, 358.6) * mm]});
            skFitSpline(sketch, "E298", {"points": [v(299.4, 358.6) * mm, v(298.84, 358.6) * mm, v(298.17, 358.64) * mm, v(297.4, 358.75) * mm]});
            skFitSpline(sketch, "E299", {"points": [v(297.4, 358.75) * mm, v(294.74, 350.17) * mm, v(293.41, 343.18) * mm, v(293.41, 337.77) * mm]});
            skFitSpline(sketch, "E300", {"points": [v(293.41, 337.77) * mm, v(293.41, 333.72) * mm, v(294.08, 330.44) * mm, v(295.4, 327.95) * mm]});
            skFitSpline(sketch, "E301", {"points": [v(295.4, 327.95) * mm, v(293.52, 325.82) * mm, v(291.53, 324.77) * mm, v(289.43, 324.77) * mm]});
            skFitSpline(sketch, "E302", {"points": [v(289.43, 324.77) * mm, v(287.44, 324.77) * mm, v(286.45, 326.37) * mm, v(286.45, 329.58) * mm]});
            skFitSpline(sketch, "E303", {"points": [v(286.45, 329.58) * mm, v(286.45, 332.7) * mm, v(287.06, 337.43) * mm, v(288.26, 343.75) * mm]});
            skFitSpline(sketch, "E304", {"points": [v(288.26, 343.75) * mm, v(282.52, 336.1) * mm, v(275.37, 332.25) * mm, v(266.85, 332.25) * mm]});
            skFitSpline(sketch, "E305", {"points": [v(266.85, 332.25) * mm, v(261.33, 332.25) * mm, v(256.9, 333.76) * mm, v(253.56, 336.78) * mm]});
            skFitSpline(sketch, "E306", {"points": [v(253.56, 336.78) * mm, v(250.21, 339.8) * mm, v(248.55, 343.84) * mm, v(248.55, 348.92) * mm]});
            skFitSpline(sketch, "E307", {"points": [v(248.55, 348.92) * mm, v(248.55, 358.85) * mm, v(254.08, 365.7) * mm, v(265.16, 369.52) * mm]});
            skFitSpline(sketch, "E308", {"points": [v(265.16, 369.52) * mm, v(261.45, 371.14) * mm, v(259.6, 374.46) * mm, v(259.6, 379.46) * mm]});
            skFitSpline(sketch, "E309", {"points": [v(259.6, 379.46) * mm, v(259.6, 383.85) * mm, v(261.34, 387.47) * mm, v(264.82, 390.34) * mm]});
            skFitSpline(sketch, "E310", {"points": [v(264.82, 390.34) * mm, v(268.3, 393.21) * mm, v(272.62, 394.65) * mm, v(277.79, 394.65) * mm]});
            skFitSpline(sketch, "E311", {"points": [v(322.46, 256.65) * mm, v(318.75, 256.65) * mm, v(315.44, 254.74) * mm, v(312.52, 250.93) * mm]});
            skFitSpline(sketch, "E312", {"points": [v(312.52, 250.93) * mm, v(309.6, 247.1) * mm, v(308.14, 242.74) * mm, v(308.14, 237.81) * mm]});
            skFitSpline(sketch, "E313", {"points": [v(308.14, 237.81) * mm, v(308.14, 234.3) * mm, v(309, 231.42) * mm, v(310.71, 229.2) * mm]});
            skFitSpline(sketch, "E314", {"points": [v(310.71, 229.2) * mm, v(312.42, 227) * mm, v(314.6, 225.9) * mm, v(317.27, 225.9) * mm]});
            skFitSpline(sketch, "E315", {"points": [v(317.27, 225.9) * mm, v(320.96, 225.9) * mm, v(324.15, 228.04) * mm, v(326.87, 232.3) * mm]});
            skFitSpline(sketch, "E316", {"points": [v(326.87, 232.3) * mm, v(329.59, 236.57) * mm, v(330.95, 241.7) * mm, v(330.95, 247.66) * mm]});
            skFitSpline(sketch, "E317", {"points": [v(330.95, 247.66) * mm, v(330.95, 249.7) * mm, v(330.7, 251.56) * mm, v(330.2, 253.23) * mm]});
            skFitSpline(sketch, "E318", {"points": [v(330.2, 253.23) * mm, v(328.41, 253.83) * mm, v(326.72, 254.85) * mm, v(325.1, 256.27) * mm]});
            skFitSpline(sketch, "E319", {"points": [v(325.1, 256.27) * mm, v(324.07, 256.52) * mm, v(323.19, 256.65) * mm, v(322.46, 256.65) * mm]});
            skFitSpline(sketch, "E320", {"points": [v(240.42, 260.48) * mm, v(237.51, 260.48) * mm, v(234.78, 258.67) * mm, v(232.23, 255.02) * mm]});
            skFitSpline(sketch, "E321", {"points": [v(232.23, 255.02) * mm, v(229.66, 251.38) * mm, v(228.07, 247.23) * mm, v(227.45, 242.57) * mm]});
            skFitSpline(sketch, "E322", {"points": [v(227.45, 242.57) * mm, v(231.63, 242.83) * mm, v(235.4, 244.32) * mm, v(238.7, 247.04) * mm]});
            skFitSpline(sketch, "E323", {"points": [v(238.7, 247.04) * mm, v(242.03, 249.75) * mm, v(243.69, 252.82) * mm, v(243.69, 256.28) * mm]});
            skFitSpline(sketch, "E324", {"points": [v(243.69, 256.28) * mm, v(243.69, 259.09) * mm, v(242.6, 260.48) * mm, v(240.42, 260.48) * mm]});
            skFitSpline(sketch, "E325", {"points": [v(241.3, 265.95) * mm, v(244.47, 265.95) * mm, v(247.04, 265.03) * mm, v(249, 263.18) * mm]});
            skFitSpline(sketch, "E326", {"points": [v(249, 263.18) * mm, v(250.95, 261.35) * mm, v(251.93, 258.88) * mm, v(251.93, 255.8) * mm]});
            skFitSpline(sketch, "E327", {"points": [v(251.93, 255.8) * mm, v(251.93, 250.86) * mm, v(249.33, 246.53) * mm, v(244.16, 242.8) * mm]});
            skFitSpline(sketch, "E328", {"points": [v(244.16, 242.8) * mm, v(238.99, 239.07) * mm, v(233.32, 237.2) * mm, v(227.17, 237.2) * mm]});
            skFitSpline(sketch, "E329", {"points": [v(227.17, 237.2) * mm, v(227.17, 230.65) * mm, v(229.8, 227.37) * mm, v(235.06, 227.37) * mm]});
            skFitSpline(sketch, "E330", {"points": [v(235.06, 227.37) * mm, v(239.89, 227.37) * mm, v(245.25, 230) * mm, v(251.17, 235.25) * mm]});
            skFitSpline(sketch, "E331", {"points": [v(251.17, 235.25) * mm, v(256.88, 240.3) * mm, v(262.17, 247.06) * mm, v(267.04, 255.52) * mm]});
            skFitSpline(sketch, "E332", {"points": [v(267.04, 255.52) * mm, v(267.04, 255.63) * mm, v(267.05, 255.74) * mm, v(267.05, 255.84) * mm]});
            skFitSpline(sketch, "E333", {"points": [v(267.05, 255.84) * mm, v(267.05, 257.15) * mm, v(266.66, 258.53) * mm, v(265.9, 260) * mm]});
            skFitSpline(sketch, "E334", {"points": [v(265.9, 260) * mm, v(268.75, 261.23) * mm, v(270.96, 261.84) * mm, v(272.57, 261.84) * mm]});
            skFitSpline(sketch, "E335", {"points": [v(272.57, 261.84) * mm, v(274.69, 261.84) * mm, v(275.75, 260.41) * mm, v(275.75, 257.56) * mm]});
            skFitSpline(sketch, "E336", {"points": [v(275.75, 257.56) * mm, v(275.75, 256.1) * mm, v(275.15, 252.22) * mm, v(273.96, 245.95) * mm]});
            skFitSpline(sketch, "E337", {"points": [v(272.03, 235.67) * mm, v(275.54, 245) * mm, v(279.56, 252.4) * mm, v(284.1, 257.82) * mm]});
            skFitSpline(sketch, "E338", {"points": [v(284.1, 257.82) * mm, v(288.64, 263.24) * mm, v(292.83, 265.95) * mm, v(296.65, 265.95) * mm]});
            skFitSpline(sketch, "E339", {"points": [v(296.65, 265.95) * mm, v(298.1, 265.95) * mm, v(299.37, 265.46) * mm, v(300.46, 264.5) * mm]});
            skFitSpline(sketch, "E340", {"points": [v(300.46, 264.5) * mm, v(301.56, 263.54) * mm, v(302.1, 262.34) * mm, v(302.1, 260.93) * mm]});
            skFitSpline(sketch, "E341", {"points": [v(302.1, 260.93) * mm, v(302.1, 258.85) * mm, v(300, 256.15) * mm, v(295.8, 252.85) * mm]});
            skFitSpline(sketch, "E342", {"points": [v(295.8, 252.85) * mm, v(294.79, 254.9) * mm, v(293.62, 255.93) * mm, v(292.3, 255.93) * mm]});
            skFitSpline(sketch, "E343", {"points": [v(292.3, 255.93) * mm, v(289.6, 255.93) * mm, v(286.03, 252.53) * mm, v(281.6, 245.7) * mm]});
            skFitSpline(sketch, "E344", {"points": [v(281.6, 245.7) * mm, v(278.8, 241.39) * mm, v(276.38, 236.93) * mm, v(274.32, 232.34) * mm]});
            skFitSpline(sketch, "E345", {"points": [v(274.32, 232.34) * mm, v(272.26, 227.76) * mm, v(271.23, 224.47) * mm, v(271.23, 222.48) * mm]});
            skLineSegment(sketch, "E346", {"start": v(273.96, 245.95) * mm, "end": v(272.03, 235.67) * mm});
            skLineSegment(sketch, "E347", {"start": v(272.03, 235.67) * mm, "end": v(273.96, 245.95) * mm});
            skFitSpline(sketch, "E348", {"points": [v(271.27, 221.52) * mm, v(269.31, 220.47) * mm, v(267.8, 219.95) * mm, v(266.72, 219.95) * mm]});
            skFitSpline(sketch, "E349", {"points": [v(266.72, 219.95) * mm, v(263.89, 219.95) * mm, v(262.46, 221.4) * mm, v(262.46, 224.27) * mm]});
            skFitSpline(sketch, "E350", {"points": [v(262.46, 224.27) * mm, v(262.46, 225.52) * mm, v(262.89, 228.56) * mm, v(263.72, 233.37) * mm]});
            skLineSegment(sketch, "E351", {"start": v(271.23, 222.48) * mm, "end": v(271.27, 221.52) * mm});
            skLineSegment(sketch, "E352", {"start": v(271.27, 221.52) * mm, "end": v(271.23, 222.48) * mm});
            skFitSpline(sketch, "E353", {"points": [v(265.47, 243.21) * mm, v(261.99, 237.94) * mm, v(257.98, 233.36) * mm, v(253.47, 229.48) * mm]});
            skFitSpline(sketch, "E354", {"points": [v(253.47, 229.48) * mm, v(246.07, 223.13) * mm, v(239.03, 219.95) * mm, v(232.34, 219.95) * mm]});
            skFitSpline(sketch, "E355", {"points": [v(232.34, 219.95) * mm, v(227.94, 219.95) * mm, v(224.47, 221.55) * mm, v(221.91, 224.73) * mm]});
            skFitSpline(sketch, "E356", {"points": [v(221.91, 224.73) * mm, v(219.35, 227.92) * mm, v(218.07, 232.24) * mm, v(218.07, 237.69) * mm]});
            skFitSpline(sketch, "E357", {"points": [v(218.07, 237.69) * mm, v(218.07, 245.46) * mm, v(220.34, 252.12) * mm, v(224.87, 257.65) * mm]});
            skFitSpline(sketch, "E358", {"points": [v(224.87, 257.65) * mm, v(229.4, 263.18) * mm, v(234.88, 265.95) * mm, v(241.3, 265.95) * mm]});
            skLineSegment(sketch, "E359", {"start": v(263.72, 233.37) * mm, "end": v(265.46, 243.12) * mm});
            skLineSegment(sketch, "E360", {"start": v(265.46, 243.12) * mm, "end": v(265.47, 243.21) * mm});
            skLineSegment(sketch, "E361", {"start": v(265.47, 243.21) * mm, "end": v(263.72, 233.37) * mm});
            skFitSpline(sketch, "E362", {"points": [v(321.7, 268.35) * mm, v(327.88, 267.8) * mm, v(332.88, 264.45) * mm, v(336.73, 258.33) * mm]});
            skFitSpline(sketch, "E363", {"points": [v(336.73, 258.33) * mm, v(340.37, 255.54) * mm, v(344.2, 254.14) * mm, v(348.24, 254.14) * mm]});
            skFitSpline(sketch, "E364", {"points": [v(348.24, 254.14) * mm, v(349.7, 254.14) * mm, v(351.28, 254.46) * mm, v(353, 255.14) * mm]});
            skFitSpline(sketch, "E365", {"points": [v(353, 255.14) * mm, v(352.25, 256.33) * mm, v(351.5, 257.44) * mm, v(350.72, 258.45) * mm]});
            skFitSpline(sketch, "E366", {"points": [v(350.72, 258.45) * mm, v(352.74, 260.55) * mm, v(354.74, 261.6) * mm, v(356.73, 261.6) * mm]});
            skFitSpline(sketch, "E367", {"points": [v(356.73, 261.6) * mm, v(358.54, 261.6) * mm, v(360, 260.73) * mm, v(361.14, 259) * mm]});
            skFitSpline(sketch, "E368", {"points": [v(361.14, 259) * mm, v(362.27, 257.26) * mm, v(363.63, 254) * mm, v(365.2, 249.2) * mm]});
            skFitSpline(sketch, "E369", {"points": [v(365.2, 249.2) * mm, v(367.64, 241.7) * mm, v(369.34, 235.1) * mm, v(370.3, 229.37) * mm]});
            skFitSpline(sketch, "E370", {"points": [v(370.3, 229.37) * mm, v(377.47, 242.97) * mm, v(381.38, 255.16) * mm, v(382.06, 265.95) * mm]});
            skFitSpline(sketch, "E371", {"points": [v(382.06, 265.95) * mm, v(387.06, 265.2) * mm, v(389.57, 263.4) * mm, v(389.57, 260.57) * mm]});
            skFitSpline(sketch, "E372", {"points": [v(389.57, 260.57) * mm, v(389.57, 257.95) * mm, v(387.72, 252.7) * mm, v(384.02, 244.83) * mm]});
            skFitSpline(sketch, "E373", {"points": [v(384.02, 244.83) * mm, v(380.32, 236.96) * mm, v(376.35, 229.75) * mm, v(372.1, 223.22) * mm]});
            skFitSpline(sketch, "E374", {"points": [v(372.1, 223.22) * mm, v(367.2, 215.7) * mm, v(362.28, 209.74) * mm, v(357.38, 205.33) * mm]});
            skFitSpline(sketch, "E375", {"points": [v(357.38, 205.33) * mm, v(352.47, 200.93) * mm, v(348.2, 198.73) * mm, v(344.57, 198.73) * mm]});
            skFitSpline(sketch, "E376", {"points": [v(344.57, 198.73) * mm, v(340.98, 198.73) * mm, v(339.18, 200.47) * mm, v(339.18, 203.94) * mm]});
            skFitSpline(sketch, "E377", {"points": [v(339.18, 203.94) * mm, v(339.18, 205.24) * mm, v(339.59, 206.91) * mm, v(340.38, 208.95) * mm]});
            skFitSpline(sketch, "E378", {"points": [v(340.38, 208.95) * mm, v(342.03, 208.07) * mm, v(343.73, 207.63) * mm, v(345.47, 207.63) * mm]});
            skFitSpline(sketch, "E379", {"points": [v(345.47, 207.63) * mm, v(352.03, 207.63) * mm, v(358.3, 212.46) * mm, v(364.27, 222.14) * mm]});
            skFitSpline(sketch, "E380", {"points": [v(364.27, 222.14) * mm, v(363.28, 228.86) * mm, v(361.54, 235.6) * mm, v(359.02, 242.38) * mm]});
            skFitSpline(sketch, "E381", {"points": [v(359.02, 242.38) * mm, v(357.95, 245.25) * mm, v(356.83, 247.88) * mm, v(355.67, 250.25) * mm]});
            skFitSpline(sketch, "E382", {"points": [v(355.67, 250.25) * mm, v(352.93, 248.72) * mm, v(350.19, 247.96) * mm, v(347.44, 247.96) * mm]});
            skFitSpline(sketch, "E383", {"points": [v(347.44, 247.96) * mm, v(344.78, 247.96) * mm, v(342.1, 248.56) * mm, v(339.4, 249.76) * mm]});
            skFitSpline(sketch, "E384", {"points": [v(339.4, 249.76) * mm, v(339.48, 249.66) * mm, v(339.5, 249.36) * mm, v(339.5, 248.87) * mm]});
            skFitSpline(sketch, "E385", {"points": [v(339.5, 248.87) * mm, v(339.5, 241.14) * mm, v(337.16, 234.38) * mm, v(332.49, 228.6) * mm]});
            skFitSpline(sketch, "E386", {"points": [v(332.49, 228.6) * mm, v(327.8, 222.83) * mm, v(322.3, 219.95) * mm, v(315.95, 219.95) * mm]});
            skFitSpline(sketch, "E387", {"points": [v(315.95, 219.95) * mm, v(311.1, 219.95) * mm, v(307.12, 221.7) * mm, v(304.05, 225.22) * mm]});
            skFitSpline(sketch, "E388", {"points": [v(304.05, 225.22) * mm, v(300.98, 228.72) * mm, v(299.44, 233.26) * mm, v(299.44, 238.82) * mm]});
            skFitSpline(sketch, "E389", {"points": [v(299.44, 238.82) * mm, v(299.44, 245.12) * mm, v(301.4, 250.58) * mm, v(305.33, 255.2) * mm]});
            skFitSpline(sketch, "E390", {"points": [v(305.33, 255.2) * mm, v(309.26, 259.81) * mm, v(313.9, 262.12) * mm, v(319.26, 262.12) * mm]});
            skFitSpline(sketch, "E391", {"points": [v(319.26, 262.12) * mm, v(320.1, 262.12) * mm, v(320.7, 262) * mm, v(321.06, 261.76) * mm]});
            skFitSpline(sketch, "E392", {"points": [v(321.06, 261.76) * mm, v(320.47, 262.26) * mm, v(320.19, 263) * mm, v(320.19, 263.94) * mm]});
            skFitSpline(sketch, "E393", {"points": [v(320.19, 263.94) * mm, v(320.19, 265.37) * mm, v(320.7, 266.85) * mm, v(321.7, 268.35) * mm]});
            skFitSpline(sketch, "E394", {"points": [v(190.94, 286.25) * mm, v(192.87, 286.25) * mm, v(193.84, 285.06) * mm, v(193.84, 282.68) * mm]});
            skFitSpline(sketch, "E395", {"points": [v(193.84, 282.68) * mm, v(193.84, 282.18) * mm, v(193.44, 279.75) * mm, v(192.63, 275.4) * mm]});
            skFitSpline(sketch, "E396", {"points": [v(186.62, 241.34) * mm, v(185.75, 236.5) * mm, v(185.32, 233.12) * mm, v(185.32, 231.22) * mm]});
            skFitSpline(sketch, "E397", {"points": [v(185.32, 231.22) * mm, v(185.32, 228.5) * mm, v(188.28, 227.13) * mm, v(194.21, 227.13) * mm]});
            skFitSpline(sketch, "E398", {"points": [v(194.21, 227.13) * mm, v(199.86, 227.13) * mm, v(206.02, 228.45) * mm, v(212.68, 231.08) * mm]});
            skFitSpline(sketch, "E399", {"points": [v(212.68, 231.08) * mm, v(211.84, 227.71) * mm, v(210.86, 225.39) * mm, v(209.73, 224.13) * mm]});
            skFitSpline(sketch, "E400", {"points": [v(209.73, 224.13) * mm, v(208.6, 222.84) * mm, v(205.85, 221.75) * mm, v(201.5, 220.86) * mm]});
            skFitSpline(sketch, "E401", {"points": [v(201.5, 220.86) * mm, v(197.16, 219.96) * mm, v(192.62, 219.5) * mm, v(187.87, 219.5) * mm]});
            skFitSpline(sketch, "E402", {"points": [v(187.87, 219.5) * mm, v(179.99, 219.5) * mm, v(176.05, 222.62) * mm, v(176.05, 228.83) * mm]});
            skFitSpline(sketch, "E403", {"points": [v(176.05, 228.83) * mm, v(176.05, 230.48) * mm, v(176.44, 233.54) * mm, v(177.24, 238.01) * mm]});
            skLineSegment(sketch, "E404", {"start": v(192.63, 275.4) * mm, "end": v(186.62, 241.34) * mm});
            skLineSegment(sketch, "E405", {"start": v(186.62, 241.34) * mm, "end": v(192.63, 275.4) * mm});
            skFitSpline(sketch, "E406", {"points": [v(184.03, 276.41) * mm, v(184.41, 278.6) * mm, v(184.6, 280.13) * mm, v(184.6, 281.03) * mm]});
            skFitSpline(sketch, "E407", {"points": [v(184.6, 281.03) * mm, v(184.6, 281.73) * mm, v(184.33, 282.67) * mm, v(183.79, 283.85) * mm]});
            skFitSpline(sketch, "E408", {"points": [v(183.79, 283.85) * mm, v(187.28, 285.45) * mm, v(189.66, 286.25) * mm, v(190.94, 286.25) * mm]});
            skLineSegment(sketch, "E409", {"start": v(177.24, 238.01) * mm, "end": v(184.03, 276.41) * mm});
            skLineSegment(sketch, "E410", {"start": v(184.03, 276.41) * mm, "end": v(177.24, 238.01) * mm});
            skFitSpline(sketch, "E411", {"points": [v(322.46, 256.65) * mm, v(318.75, 256.65) * mm, v(315.44, 254.74) * mm, v(312.52, 250.93) * mm]});
            skFitSpline(sketch, "E412", {"points": [v(312.52, 250.93) * mm, v(309.6, 247.1) * mm, v(308.14, 242.74) * mm, v(308.14, 237.81) * mm]});
            skFitSpline(sketch, "E413", {"points": [v(308.14, 237.81) * mm, v(308.14, 234.3) * mm, v(309, 231.42) * mm, v(310.71, 229.2) * mm]});
            skFitSpline(sketch, "E414", {"points": [v(310.71, 229.2) * mm, v(312.42, 227) * mm, v(314.6, 225.9) * mm, v(317.27, 225.9) * mm]});
            skFitSpline(sketch, "E415", {"points": [v(317.27, 225.9) * mm, v(320.96, 225.9) * mm, v(324.15, 228.04) * mm, v(326.87, 232.3) * mm]});
            skFitSpline(sketch, "E416", {"points": [v(326.87, 232.3) * mm, v(329.59, 236.57) * mm, v(330.95, 241.7) * mm, v(330.95, 247.66) * mm]});
            skFitSpline(sketch, "E417", {"points": [v(330.95, 247.66) * mm, v(330.95, 249.7) * mm, v(330.7, 251.56) * mm, v(330.2, 253.23) * mm]});
            skFitSpline(sketch, "E418", {"points": [v(330.2, 253.23) * mm, v(328.41, 253.83) * mm, v(326.72, 254.85) * mm, v(325.1, 256.27) * mm]});
            skFitSpline(sketch, "E419", {"points": [v(325.1, 256.27) * mm, v(324.07, 256.52) * mm, v(323.19, 256.65) * mm, v(322.46, 256.65) * mm]});
            skFitSpline(sketch, "E420", {"points": [v(240.42, 260.48) * mm, v(237.51, 260.48) * mm, v(234.78, 258.67) * mm, v(232.23, 255.02) * mm]});
            skFitSpline(sketch, "E421", {"points": [v(232.23, 255.02) * mm, v(229.66, 251.38) * mm, v(228.07, 247.23) * mm, v(227.45, 242.57) * mm]});
            skFitSpline(sketch, "E422", {"points": [v(227.45, 242.57) * mm, v(231.63, 242.83) * mm, v(235.4, 244.32) * mm, v(238.7, 247.04) * mm]});
            skFitSpline(sketch, "E423", {"points": [v(238.7, 247.04) * mm, v(242.03, 249.75) * mm, v(243.69, 252.82) * mm, v(243.69, 256.28) * mm]});
            skFitSpline(sketch, "E424", {"points": [v(243.69, 256.28) * mm, v(243.69, 259.09) * mm, v(242.6, 260.48) * mm, v(240.42, 260.48) * mm]});
            skFitSpline(sketch, "E425", {"points": [v(241.3, 265.95) * mm, v(244.47, 265.95) * mm, v(247.04, 265.03) * mm, v(249, 263.18) * mm]});
            skFitSpline(sketch, "E426", {"points": [v(249, 263.18) * mm, v(250.95, 261.35) * mm, v(251.93, 258.88) * mm, v(251.93, 255.8) * mm]});
            skFitSpline(sketch, "E427", {"points": [v(251.93, 255.8) * mm, v(251.93, 250.86) * mm, v(249.33, 246.53) * mm, v(244.16, 242.8) * mm]});
            skFitSpline(sketch, "E428", {"points": [v(244.16, 242.8) * mm, v(238.99, 239.07) * mm, v(233.32, 237.2) * mm, v(227.17, 237.2) * mm]});
            skFitSpline(sketch, "E429", {"points": [v(227.17, 237.2) * mm, v(227.17, 230.65) * mm, v(229.8, 227.37) * mm, v(235.06, 227.37) * mm]});
            skFitSpline(sketch, "E430", {"points": [v(235.06, 227.37) * mm, v(239.89, 227.37) * mm, v(245.25, 230) * mm, v(251.17, 235.25) * mm]});
            skFitSpline(sketch, "E431", {"points": [v(251.17, 235.25) * mm, v(256.88, 240.3) * mm, v(262.17, 247.06) * mm, v(267.04, 255.52) * mm]});
            skFitSpline(sketch, "E432", {"points": [v(267.04, 255.52) * mm, v(267.04, 255.63) * mm, v(267.05, 255.74) * mm, v(267.05, 255.84) * mm]});
            skFitSpline(sketch, "E433", {"points": [v(267.05, 255.84) * mm, v(267.05, 257.15) * mm, v(266.66, 258.53) * mm, v(265.9, 260) * mm]});
            skFitSpline(sketch, "E434", {"points": [v(265.9, 260) * mm, v(268.75, 261.23) * mm, v(270.96, 261.84) * mm, v(272.57, 261.84) * mm]});
            skFitSpline(sketch, "E435", {"points": [v(272.57, 261.84) * mm, v(274.69, 261.84) * mm, v(275.75, 260.41) * mm, v(275.75, 257.56) * mm]});
            skFitSpline(sketch, "E436", {"points": [v(275.75, 257.56) * mm, v(275.75, 256.1) * mm, v(275.15, 252.22) * mm, v(273.96, 245.95) * mm]});
            skFitSpline(sketch, "E437", {"points": [v(272.03, 235.67) * mm, v(275.54, 245) * mm, v(279.56, 252.4) * mm, v(284.1, 257.82) * mm]});
            skFitSpline(sketch, "E438", {"points": [v(284.1, 257.82) * mm, v(288.64, 263.24) * mm, v(292.83, 265.95) * mm, v(296.65, 265.95) * mm]});
            skFitSpline(sketch, "E439", {"points": [v(296.65, 265.95) * mm, v(298.1, 265.95) * mm, v(299.37, 265.46) * mm, v(300.46, 264.5) * mm]});
            skFitSpline(sketch, "E440", {"points": [v(300.46, 264.5) * mm, v(301.56, 263.54) * mm, v(302.1, 262.34) * mm, v(302.1, 260.93) * mm]});
            skFitSpline(sketch, "E441", {"points": [v(302.1, 260.93) * mm, v(302.1, 258.85) * mm, v(300, 256.15) * mm, v(295.8, 252.85) * mm]});
            skFitSpline(sketch, "E442", {"points": [v(295.8, 252.85) * mm, v(294.79, 254.9) * mm, v(293.62, 255.93) * mm, v(292.3, 255.93) * mm]});
            skFitSpline(sketch, "E443", {"points": [v(292.3, 255.93) * mm, v(289.6, 255.93) * mm, v(286.03, 252.53) * mm, v(281.6, 245.7) * mm]});
            skFitSpline(sketch, "E444", {"points": [v(281.6, 245.7) * mm, v(278.8, 241.39) * mm, v(276.38, 236.93) * mm, v(274.32, 232.34) * mm]});
            skFitSpline(sketch, "E445", {"points": [v(274.32, 232.34) * mm, v(272.26, 227.76) * mm, v(271.23, 224.47) * mm, v(271.23, 222.48) * mm]});
            skFitSpline(sketch, "E446", {"points": [v(271.27, 221.52) * mm, v(269.31, 220.47) * mm, v(267.8, 219.95) * mm, v(266.72, 219.95) * mm]});
            skFitSpline(sketch, "E447", {"points": [v(266.72, 219.95) * mm, v(263.89, 219.95) * mm, v(262.46, 221.4) * mm, v(262.46, 224.27) * mm]});
            skFitSpline(sketch, "E448", {"points": [v(262.46, 224.27) * mm, v(262.46, 225.52) * mm, v(262.89, 228.56) * mm, v(263.72, 233.37) * mm]});
            skFitSpline(sketch, "E449", {"points": [v(265.47, 243.21) * mm, v(261.99, 237.94) * mm, v(257.98, 233.36) * mm, v(253.47, 229.48) * mm]});
            skFitSpline(sketch, "E450", {"points": [v(253.47, 229.48) * mm, v(246.07, 223.13) * mm, v(239.03, 219.95) * mm, v(232.34, 219.95) * mm]});
            skFitSpline(sketch, "E451", {"points": [v(232.34, 219.95) * mm, v(227.94, 219.95) * mm, v(224.47, 221.55) * mm, v(221.91, 224.73) * mm]});
            skFitSpline(sketch, "E452", {"points": [v(221.91, 224.73) * mm, v(219.35, 227.92) * mm, v(218.07, 232.24) * mm, v(218.07, 237.69) * mm]});
            skFitSpline(sketch, "E453", {"points": [v(218.07, 237.69) * mm, v(218.07, 245.46) * mm, v(220.34, 252.12) * mm, v(224.87, 257.65) * mm]});
            skFitSpline(sketch, "E454", {"points": [v(224.87, 257.65) * mm, v(229.4, 263.18) * mm, v(234.88, 265.95) * mm, v(241.3, 265.95) * mm]});
            skFitSpline(sketch, "E455", {"points": [v(321.7, 268.35) * mm, v(327.88, 267.8) * mm, v(332.88, 264.45) * mm, v(336.73, 258.33) * mm]});
            skFitSpline(sketch, "E456", {"points": [v(336.73, 258.33) * mm, v(340.37, 255.54) * mm, v(344.2, 254.14) * mm, v(348.24, 254.14) * mm]});
            skFitSpline(sketch, "E457", {"points": [v(348.24, 254.14) * mm, v(349.7, 254.14) * mm, v(351.28, 254.46) * mm, v(353, 255.14) * mm]});
            skFitSpline(sketch, "E458", {"points": [v(353, 255.14) * mm, v(352.25, 256.33) * mm, v(351.5, 257.44) * mm, v(350.72, 258.45) * mm]});
            skFitSpline(sketch, "E459", {"points": [v(350.72, 258.45) * mm, v(352.74, 260.55) * mm, v(354.74, 261.6) * mm, v(356.73, 261.6) * mm]});
            skFitSpline(sketch, "E460", {"points": [v(356.73, 261.6) * mm, v(358.54, 261.6) * mm, v(360, 260.73) * mm, v(361.14, 259) * mm]});
            skFitSpline(sketch, "E461", {"points": [v(361.14, 259) * mm, v(362.27, 257.26) * mm, v(363.63, 254) * mm, v(365.2, 249.2) * mm]});
            skFitSpline(sketch, "E462", {"points": [v(365.2, 249.2) * mm, v(367.64, 241.7) * mm, v(369.34, 235.1) * mm, v(370.3, 229.37) * mm]});
            skFitSpline(sketch, "E463", {"points": [v(370.3, 229.37) * mm, v(377.47, 242.97) * mm, v(381.38, 255.16) * mm, v(382.06, 265.95) * mm]});
            skFitSpline(sketch, "E464", {"points": [v(382.06, 265.95) * mm, v(387.06, 265.2) * mm, v(389.57, 263.4) * mm, v(389.57, 260.57) * mm]});
            skFitSpline(sketch, "E465", {"points": [v(389.57, 260.57) * mm, v(389.57, 257.95) * mm, v(387.72, 252.7) * mm, v(384.02, 244.83) * mm]});
            skFitSpline(sketch, "E466", {"points": [v(384.02, 244.83) * mm, v(380.32, 236.96) * mm, v(376.35, 229.75) * mm, v(372.1, 223.22) * mm]});
            skFitSpline(sketch, "E467", {"points": [v(372.1, 223.22) * mm, v(367.2, 215.7) * mm, v(362.28, 209.74) * mm, v(357.38, 205.33) * mm]});
            skFitSpline(sketch, "E468", {"points": [v(357.38, 205.33) * mm, v(352.47, 200.93) * mm, v(348.2, 198.73) * mm, v(344.57, 198.73) * mm]});
            skFitSpline(sketch, "E469", {"points": [v(344.57, 198.73) * mm, v(340.98, 198.73) * mm, v(339.18, 200.47) * mm, v(339.18, 203.94) * mm]});
            skFitSpline(sketch, "E470", {"points": [v(339.18, 203.94) * mm, v(339.18, 205.24) * mm, v(339.59, 206.91) * mm, v(340.38, 208.95) * mm]});
            skFitSpline(sketch, "E471", {"points": [v(340.38, 208.95) * mm, v(342.03, 208.07) * mm, v(343.73, 207.63) * mm, v(345.47, 207.63) * mm]});
            skFitSpline(sketch, "E472", {"points": [v(345.47, 207.63) * mm, v(352.03, 207.63) * mm, v(358.3, 212.46) * mm, v(364.27, 222.14) * mm]});
            skFitSpline(sketch, "E473", {"points": [v(364.27, 222.14) * mm, v(363.28, 228.86) * mm, v(361.54, 235.6) * mm, v(359.02, 242.38) * mm]});
            skFitSpline(sketch, "E474", {"points": [v(359.02, 242.38) * mm, v(357.95, 245.25) * mm, v(356.83, 247.88) * mm, v(355.67, 250.25) * mm]});
            skFitSpline(sketch, "E475", {"points": [v(355.67, 250.25) * mm, v(352.93, 248.72) * mm, v(350.19, 247.96) * mm, v(347.44, 247.96) * mm]});
            skFitSpline(sketch, "E476", {"points": [v(347.44, 247.96) * mm, v(344.78, 247.96) * mm, v(342.1, 248.56) * mm, v(339.4, 249.76) * mm]});
            skFitSpline(sketch, "E477", {"points": [v(339.4, 249.76) * mm, v(339.48, 249.66) * mm, v(339.5, 249.36) * mm, v(339.5, 248.87) * mm]});
            skFitSpline(sketch, "E478", {"points": [v(339.5, 248.87) * mm, v(339.5, 241.14) * mm, v(337.16, 234.38) * mm, v(332.49, 228.6) * mm]});
            skFitSpline(sketch, "E479", {"points": [v(332.49, 228.6) * mm, v(327.8, 222.83) * mm, v(322.3, 219.95) * mm, v(315.95, 219.95) * mm]});
            skFitSpline(sketch, "E480", {"points": [v(315.95, 219.95) * mm, v(311.1, 219.95) * mm, v(307.12, 221.7) * mm, v(304.05, 225.22) * mm]});
            skFitSpline(sketch, "E481", {"points": [v(304.05, 225.22) * mm, v(300.98, 228.72) * mm, v(299.44, 233.26) * mm, v(299.44, 238.82) * mm]});
            skFitSpline(sketch, "E482", {"points": [v(299.44, 238.82) * mm, v(299.44, 245.12) * mm, v(301.4, 250.58) * mm, v(305.33, 255.2) * mm]});
            skFitSpline(sketch, "E483", {"points": [v(305.33, 255.2) * mm, v(309.26, 259.81) * mm, v(313.9, 262.12) * mm, v(319.26, 262.12) * mm]});
            skFitSpline(sketch, "E484", {"points": [v(319.26, 262.12) * mm, v(320.1, 262.12) * mm, v(320.7, 262) * mm, v(321.06, 261.76) * mm]});
            skFitSpline(sketch, "E485", {"points": [v(321.06, 261.76) * mm, v(320.47, 262.26) * mm, v(320.19, 263) * mm, v(320.19, 263.94) * mm]});
            skFitSpline(sketch, "E486", {"points": [v(320.19, 263.94) * mm, v(320.19, 265.37) * mm, v(320.7, 266.85) * mm, v(321.7, 268.35) * mm]});
            skFitSpline(sketch, "E487", {"points": [v(190.94, 286.25) * mm, v(192.87, 286.25) * mm, v(193.84, 285.06) * mm, v(193.84, 282.68) * mm]});
            skFitSpline(sketch, "E488", {"points": [v(193.84, 282.68) * mm, v(193.84, 282.18) * mm, v(193.44, 279.75) * mm, v(192.63, 275.4) * mm]});
            skFitSpline(sketch, "E489", {"points": [v(186.62, 241.34) * mm, v(185.75, 236.5) * mm, v(185.32, 233.12) * mm, v(185.32, 231.22) * mm]});
            skFitSpline(sketch, "E490", {"points": [v(185.32, 231.22) * mm, v(185.32, 228.5) * mm, v(188.28, 227.13) * mm, v(194.21, 227.13) * mm]});
            skFitSpline(sketch, "E491", {"points": [v(194.21, 227.13) * mm, v(199.86, 227.13) * mm, v(206.02, 228.45) * mm, v(212.68, 231.08) * mm]});
            skFitSpline(sketch, "E492", {"points": [v(212.68, 231.08) * mm, v(211.84, 227.71) * mm, v(210.86, 225.39) * mm, v(209.73, 224.13) * mm]});
            skFitSpline(sketch, "E493", {"points": [v(209.73, 224.13) * mm, v(208.6, 222.84) * mm, v(205.85, 221.75) * mm, v(201.5, 220.86) * mm]});
            skFitSpline(sketch, "E494", {"points": [v(201.5, 220.86) * mm, v(197.16, 219.96) * mm, v(192.62, 219.5) * mm, v(187.87, 219.5) * mm]});
            skFitSpline(sketch, "E495", {"points": [v(187.87, 219.5) * mm, v(179.99, 219.5) * mm, v(176.05, 222.62) * mm, v(176.05, 228.83) * mm]});
            skFitSpline(sketch, "E496", {"points": [v(176.05, 228.83) * mm, v(176.05, 230.48) * mm, v(176.44, 233.54) * mm, v(177.24, 238.01) * mm]});
            skFitSpline(sketch, "E497", {"points": [v(184.03, 276.41) * mm, v(184.41, 278.6) * mm, v(184.6, 280.13) * mm, v(184.6, 281.03) * mm]});
            skFitSpline(sketch, "E498", {"points": [v(184.6, 281.03) * mm, v(184.6, 281.73) * mm, v(184.33, 282.67) * mm, v(183.79, 283.85) * mm]});
            skFitSpline(sketch, "E499", {"points": [v(183.79, 283.85) * mm, v(187.28, 285.45) * mm, v(189.66, 286.25) * mm, v(190.94, 286.25) * mm]});
            skFitSpline(sketch, "E500", {"points": [v(148.9, 160.76) * mm, v(152.84, 160.76) * mm, v(156.03, 159.69) * mm, v(158.5, 157.52) * mm]});
            skFitSpline(sketch, "E501", {"points": [v(158.5, 157.52) * mm, v(160.96, 155.36) * mm, v(162.2, 152.5) * mm, v(162.2, 148.95) * mm]});
            skFitSpline(sketch, "E502", {"points": [v(162.2, 148.95) * mm, v(162.2, 139.05) * mm, v(152.73, 125.67) * mm, v(133.82, 108.83) * mm]});
            skFitSpline(sketch, "E503", {"points": [v(133.82, 108.83) * mm, v(141.2, 110.02) * mm, v(147.51, 110.62) * mm, v(152.72, 110.62) * mm]});
            skFitSpline(sketch, "E504", {"points": [v(152.72, 110.62) * mm, v(156.78, 110.62) * mm, v(159.46, 109.94) * mm, v(160.79, 108.57) * mm]});
            skFitSpline(sketch, "E505", {"points": [v(160.79, 108.57) * mm, v(162.11, 107.2) * mm, v(162.93, 103.95) * mm, v(163.25, 98.82) * mm]});
            skFitSpline(sketch, "E506", {"points": [v(163.25, 98.82) * mm, v(159.1, 100.65) * mm, v(154.02, 101.57) * mm, v(148.06, 101.57) * mm]});
            skFitSpline(sketch, "E507", {"points": [v(148.06, 101.57) * mm, v(143.16, 101.57) * mm, v(138.24, 101.13) * mm, v(133.32, 100.27) * mm]});
            skFitSpline(sketch, "E508", {"points": [v(131.2, 99.92) * mm, v(129.2, 99.58) * mm, v(127.89, 99.4) * mm, v(127.26, 99.4) * mm]});
            skFitSpline(sketch, "E509", {"points": [v(127.26, 99.4) * mm, v(125.1, 99.4) * mm, v(124.04, 100.8) * mm, v(124.04, 103.6) * mm]});
            skFitSpline(sketch, "E510", {"points": [v(124.04, 103.6) * mm, v(124.04, 104.4) * mm, v(124.14, 105.62) * mm, v(124.32, 107.24) * mm]});
            skFitSpline(sketch, "E511", {"points": [v(124.32, 107.24) * mm, v(132.32, 113.12) * mm, v(139.12, 119.9) * mm, v(144.71, 127.63) * mm]});
            skFitSpline(sketch, "E512", {"points": [v(144.71, 127.63) * mm, v(150.3, 135.35) * mm, v(153.1, 141.66) * mm, v(153.1, 146.57) * mm]});
            skFitSpline(sketch, "E513", {"points": [v(153.1, 146.57) * mm, v(153.1, 151.09) * mm, v(150.85, 153.34) * mm, v(146.35, 153.34) * mm]});
            skFitSpline(sketch, "E514", {"points": [v(146.35, 153.34) * mm, v(140.98, 153.34) * mm, v(135.91, 149.75) * mm, v(131.13, 142.53) * mm]});
            skFitSpline(sketch, "E515", {"points": [v(131.13, 142.53) * mm, v(130.6, 144.51) * mm, v(130.34, 146) * mm, v(130.34, 147.01) * mm]});
            skFitSpline(sketch, "E516", {"points": [v(130.34, 147.01) * mm, v(130.34, 150.43) * mm, v(132.32, 153.57) * mm, v(136.28, 156.45) * mm]});
            skFitSpline(sketch, "E517", {"points": [v(136.28, 156.45) * mm, v(140.24, 159.33) * mm, v(144.45, 160.76) * mm, v(148.9, 160.76) * mm]});
            skLineSegment(sketch, "E518", {"start": v(133.32, 100.27) * mm, "end": v(131.2, 99.92) * mm});
            skLineSegment(sketch, "E519", {"start": v(131.2, 99.92) * mm, "end": v(133.32, 100.27) * mm});
            skFitSpline(sketch, "E520", {"points": [v(148.9, 160.76) * mm, v(152.84, 160.76) * mm, v(156.03, 159.69) * mm, v(158.5, 157.52) * mm]});
            skFitSpline(sketch, "E521", {"points": [v(158.5, 157.52) * mm, v(160.96, 155.36) * mm, v(162.2, 152.5) * mm, v(162.2, 148.95) * mm]});
            skFitSpline(sketch, "E522", {"points": [v(162.2, 148.95) * mm, v(162.2, 139.05) * mm, v(152.73, 125.67) * mm, v(133.82, 108.83) * mm]});
            skFitSpline(sketch, "E523", {"points": [v(133.82, 108.83) * mm, v(141.2, 110.02) * mm, v(147.51, 110.62) * mm, v(152.72, 110.62) * mm]});
            skFitSpline(sketch, "E524", {"points": [v(152.72, 110.62) * mm, v(156.78, 110.62) * mm, v(159.46, 109.94) * mm, v(160.79, 108.57) * mm]});
            skFitSpline(sketch, "E525", {"points": [v(160.79, 108.57) * mm, v(162.11, 107.2) * mm, v(162.93, 103.95) * mm, v(163.25, 98.82) * mm]});
            skFitSpline(sketch, "E526", {"points": [v(163.25, 98.82) * mm, v(159.1, 100.65) * mm, v(154.02, 101.57) * mm, v(148.06, 101.57) * mm]});
            skFitSpline(sketch, "E527", {"points": [v(148.06, 101.57) * mm, v(143.16, 101.57) * mm, v(138.24, 101.13) * mm, v(133.32, 100.27) * mm]});
            skFitSpline(sketch, "E528", {"points": [v(131.2, 99.92) * mm, v(129.2, 99.58) * mm, v(127.89, 99.4) * mm, v(127.26, 99.4) * mm]});
            skFitSpline(sketch, "E529", {"points": [v(127.26, 99.4) * mm, v(125.1, 99.4) * mm, v(124.04, 100.8) * mm, v(124.04, 103.6) * mm]});
            skFitSpline(sketch, "E530", {"points": [v(124.04, 103.6) * mm, v(124.04, 104.4) * mm, v(124.14, 105.62) * mm, v(124.32, 107.24) * mm]});
            skFitSpline(sketch, "E531", {"points": [v(124.32, 107.24) * mm, v(132.32, 113.12) * mm, v(139.12, 119.9) * mm, v(144.71, 127.63) * mm]});
            skFitSpline(sketch, "E532", {"points": [v(144.71, 127.63) * mm, v(150.3, 135.35) * mm, v(153.1, 141.66) * mm, v(153.1, 146.57) * mm]});
            skFitSpline(sketch, "E533", {"points": [v(153.1, 146.57) * mm, v(153.1, 151.09) * mm, v(150.85, 153.34) * mm, v(146.35, 153.34) * mm]});
            skFitSpline(sketch, "E534", {"points": [v(146.35, 153.34) * mm, v(140.98, 153.34) * mm, v(135.91, 149.75) * mm, v(131.13, 142.53) * mm]});
            skFitSpline(sketch, "E535", {"points": [v(131.13, 142.53) * mm, v(130.6, 144.51) * mm, v(130.34, 146) * mm, v(130.34, 147.01) * mm]});
            skFitSpline(sketch, "E536", {"points": [v(130.34, 147.01) * mm, v(130.34, 150.43) * mm, v(132.32, 153.57) * mm, v(136.28, 156.45) * mm]});
            skFitSpline(sketch, "E537", {"points": [v(136.28, 156.45) * mm, v(140.24, 159.33) * mm, v(144.45, 160.76) * mm, v(148.9, 160.76) * mm]});
            skFitSpline(sketch, "E538", {"points": [v(202.2, 129.7) * mm, v(201.44, 123.52) * mm, v(199.56, 120.44) * mm, v(196.58, 120.44) * mm]});
            skFitSpline(sketch, "E539", {"points": [v(196.58, 120.44) * mm, v(195.93, 120.44) * mm, v(195.18, 120.5) * mm, v(194.33, 120.6) * mm]});
            skFitSpline(sketch, "E540", {"points": [v(191.57, 120.98) * mm, v(189.87, 121.23) * mm, v(188.55, 121.35) * mm, v(187.62, 121.35) * mm]});
            skFitSpline(sketch, "E541", {"points": [v(187.62, 121.35) * mm, v(186.31, 121.35) * mm, v(184.66, 120.96) * mm, v(182.65, 120.15) * mm]});
            skFitSpline(sketch, "E542", {"points": [v(182.65, 120.15) * mm, v(184.1, 125.83) * mm, v(186.47, 128.65) * mm, v(189.74, 128.65) * mm]});
            skFitSpline(sketch, "E543", {"points": [v(189.74, 128.65) * mm, v(190.3, 128.65) * mm, v(190.9, 128.6) * mm, v(191.57, 128.53) * mm]});
            skLineSegment(sketch, "E544", {"start": v(194.33, 120.6) * mm, "end": v(191.57, 120.98) * mm});
            skLineSegment(sketch, "E545", {"start": v(191.57, 120.98) * mm, "end": v(194.33, 120.6) * mm});
            skFitSpline(sketch, "E546", {"points": [v(195.42, 128.04) * mm, v(196.04, 127.97) * mm, v(196.72, 127.94) * mm, v(197.45, 127.94) * mm]});
            skFitSpline(sketch, "E547", {"points": [v(197.45, 127.94) * mm, v(199.07, 127.94) * mm, v(200.66, 128.53) * mm, v(202.2, 129.7) * mm]});
            skLineSegment(sketch, "E548", {"start": v(191.57, 128.53) * mm, "end": v(195.42, 128.04) * mm});
            skLineSegment(sketch, "E549", {"start": v(195.42, 128.04) * mm, "end": v(191.57, 128.53) * mm});
            skFitSpline(sketch, "E550", {"points": [v(202.2, 129.7) * mm, v(201.44, 123.52) * mm, v(199.56, 120.44) * mm, v(196.58, 120.44) * mm]});
            skFitSpline(sketch, "E551", {"points": [v(196.58, 120.44) * mm, v(195.93, 120.44) * mm, v(195.18, 120.5) * mm, v(194.33, 120.6) * mm]});
            skFitSpline(sketch, "E552", {"points": [v(191.57, 120.98) * mm, v(189.87, 121.23) * mm, v(188.55, 121.35) * mm, v(187.62, 121.35) * mm]});
            skFitSpline(sketch, "E553", {"points": [v(187.62, 121.35) * mm, v(186.31, 121.35) * mm, v(184.66, 120.96) * mm, v(182.65, 120.15) * mm]});
            skFitSpline(sketch, "E554", {"points": [v(182.65, 120.15) * mm, v(184.1, 125.83) * mm, v(186.47, 128.65) * mm, v(189.74, 128.65) * mm]});
            skFitSpline(sketch, "E555", {"points": [v(189.74, 128.65) * mm, v(190.3, 128.65) * mm, v(190.9, 128.6) * mm, v(191.57, 128.53) * mm]});
            skFitSpline(sketch, "E556", {"points": [v(195.42, 128.04) * mm, v(196.04, 127.97) * mm, v(196.72, 127.94) * mm, v(197.45, 127.94) * mm]});
            skFitSpline(sketch, "E557", {"points": [v(197.45, 127.94) * mm, v(199.07, 127.94) * mm, v(200.66, 128.53) * mm, v(202.2, 129.7) * mm]});
            skFitSpline(sketch, "E558", {"points": [v(231.1, 107.4) * mm, v(233.12, 107.8) * mm, v(234.8, 107.99) * mm, v(236.16, 107.99) * mm]});
            skFitSpline(sketch, "E559", {"points": [v(236.16, 107.99) * mm, v(239.42, 107.99) * mm, v(241.64, 107.39) * mm, v(242.8, 106.17) * mm]});
            skFitSpline(sketch, "E560", {"points": [v(242.8, 106.17) * mm, v(243.98, 104.96) * mm, v(244.56, 102.4) * mm, v(244.56, 98.48) * mm]});
            skFitSpline(sketch, "E561", {"points": [v(244.56, 98.48) * mm, v(242.68, 99.4) * mm, v(240.77, 99.85) * mm, v(238.84, 99.85) * mm]});
            skFitSpline(sketch, "E562", {"points": [v(238.84, 99.85) * mm, v(236.6, 99.85) * mm, v(233.83, 99.62) * mm, v(230.56, 99.18) * mm]});
            skLineSegment(sketch, "E563", {"start": v(240.33, 160.84) * mm, "end": v(231.1, 107.4) * mm});
            skLineSegment(sketch, "E564", {"start": v(231.1, 107.4) * mm, "end": v(240.33, 160.84) * mm});
            skFitSpline(sketch, "E565", {"points": [v(225.68, 98.5) * mm, v(224.08, 98.26) * mm, v(221.9, 97.9) * mm, v(219.13, 97.41) * mm]});
            skFitSpline(sketch, "E566", {"points": [v(219.13, 97.41) * mm, v(218.25, 97.25) * mm, v(217.34, 97.17) * mm, v(216.4, 97.17) * mm]});
            skFitSpline(sketch, "E567", {"points": [v(216.4, 97.17) * mm, v(213.42, 97.17) * mm, v(211.7, 100.17) * mm, v(211.24, 106.14) * mm]});
            skFitSpline(sketch, "E568", {"points": [v(211.24, 106.14) * mm, v(213.04, 105.46) * mm, v(214.48, 105.12) * mm, v(215.58, 105.12) * mm]});
            skFitSpline(sketch, "E569", {"points": [v(215.58, 105.12) * mm, v(218.04, 105.12) * mm, v(220.36, 105.41) * mm, v(222.57, 106) * mm]});
            skLineSegment(sketch, "E570", {"start": v(230.56, 99.18) * mm, "end": v(225.68, 98.5) * mm});
            skLineSegment(sketch, "E571", {"start": v(225.68, 98.5) * mm, "end": v(230.56, 99.18) * mm});
            skFitSpline(sketch, "E572", {"points": [v(230.14, 148.1) * mm, v(226.91, 146) * mm, v(224.12, 144.93) * mm, v(221.77, 144.93) * mm]});
            skFitSpline(sketch, "E573", {"points": [v(221.77, 144.93) * mm, v(217.95, 144.93) * mm, v(216.04, 147.62) * mm, v(216.04, 153.01) * mm]});
            skLineSegment(sketch, "E574", {"start": v(222.57, 106) * mm, "end": v(230.14, 148.1) * mm});
            skLineSegment(sketch, "E575", {"start": v(230.14, 148.1) * mm, "end": v(222.57, 106) * mm});
            skFitSpline(sketch, "E576", {"points": [v(216.04, 154.9) * mm, v(218.1, 153.52) * mm, v(219.94, 152.83) * mm, v(221.59, 152.83) * mm]});
            skFitSpline(sketch, "E577", {"points": [v(221.59, 152.83) * mm, v(224.5, 152.83) * mm, v(229.56, 155.03) * mm, v(236.73, 159.44) * mm]});
            skFitSpline(sketch, "E578", {"points": [v(236.73, 159.44) * mm, v(237.05, 159.62) * mm, v(238.25, 160.1) * mm, v(240.33, 160.84) * mm]});
            skLineSegment(sketch, "E579", {"start": v(216.04, 153.01) * mm, "end": v(216.04, 154.9) * mm});
            skLineSegment(sketch, "E580", {"start": v(216.04, 154.9) * mm, "end": v(216.04, 153.01) * mm});
            skFitSpline(sketch, "E581", {"points": [v(231.1, 107.4) * mm, v(233.12, 107.8) * mm, v(234.8, 107.99) * mm, v(236.16, 107.99) * mm]});
            skFitSpline(sketch, "E582", {"points": [v(236.16, 107.99) * mm, v(239.42, 107.99) * mm, v(241.64, 107.39) * mm, v(242.8, 106.17) * mm]});
            skFitSpline(sketch, "E583", {"points": [v(242.8, 106.17) * mm, v(243.98, 104.96) * mm, v(244.56, 102.4) * mm, v(244.56, 98.48) * mm]});
            skFitSpline(sketch, "E584", {"points": [v(244.56, 98.48) * mm, v(242.68, 99.4) * mm, v(240.77, 99.85) * mm, v(238.84, 99.85) * mm]});
            skFitSpline(sketch, "E585", {"points": [v(238.84, 99.85) * mm, v(236.6, 99.85) * mm, v(233.83, 99.62) * mm, v(230.56, 99.18) * mm]});
            skFitSpline(sketch, "E586", {"points": [v(225.68, 98.5) * mm, v(224.08, 98.26) * mm, v(221.9, 97.9) * mm, v(219.13, 97.41) * mm]});
            skFitSpline(sketch, "E587", {"points": [v(219.13, 97.41) * mm, v(218.25, 97.25) * mm, v(217.34, 97.17) * mm, v(216.4, 97.17) * mm]});
            skFitSpline(sketch, "E588", {"points": [v(216.4, 97.17) * mm, v(213.42, 97.17) * mm, v(211.7, 100.17) * mm, v(211.24, 106.14) * mm]});
            skFitSpline(sketch, "E589", {"points": [v(211.24, 106.14) * mm, v(213.04, 105.46) * mm, v(214.48, 105.12) * mm, v(215.58, 105.12) * mm]});
            skFitSpline(sketch, "E590", {"points": [v(215.58, 105.12) * mm, v(218.04, 105.12) * mm, v(220.36, 105.41) * mm, v(222.57, 106) * mm]});
            skFitSpline(sketch, "E591", {"points": [v(230.14, 148.1) * mm, v(226.91, 146) * mm, v(224.12, 144.93) * mm, v(221.77, 144.93) * mm]});
            skFitSpline(sketch, "E592", {"points": [v(221.77, 144.93) * mm, v(217.95, 144.93) * mm, v(216.04, 147.62) * mm, v(216.04, 153.01) * mm]});
            skFitSpline(sketch, "E593", {"points": [v(216.04, 154.9) * mm, v(218.1, 153.52) * mm, v(219.94, 152.83) * mm, v(221.59, 152.83) * mm]});
            skFitSpline(sketch, "E594", {"points": [v(221.59, 152.83) * mm, v(224.5, 152.83) * mm, v(229.56, 155.03) * mm, v(236.73, 159.44) * mm]});
            skFitSpline(sketch, "E595", {"points": [v(236.73, 159.44) * mm, v(237.05, 159.62) * mm, v(238.25, 160.1) * mm, v(240.33, 160.84) * mm]});
            skFitSpline(sketch, "E596", {"points": [v(280.08, 107.4) * mm, v(282.1, 107.8) * mm, v(283.8, 107.99) * mm, v(285.15, 107.99) * mm]});
            skFitSpline(sketch, "E597", {"points": [v(285.15, 107.99) * mm, v(288.4, 107.99) * mm, v(290.62, 107.39) * mm, v(291.8, 106.17) * mm]});
            skFitSpline(sketch, "E598", {"points": [v(291.8, 106.17) * mm, v(292.97, 104.96) * mm, v(293.54, 102.4) * mm, v(293.54, 98.48) * mm]});
            skFitSpline(sketch, "E599", {"points": [v(293.54, 98.48) * mm, v(291.66, 99.4) * mm, v(289.75, 99.85) * mm, v(287.82, 99.85) * mm]});
            skFitSpline(sketch, "E600", {"points": [v(287.82, 99.85) * mm, v(285.58, 99.85) * mm, v(282.82, 99.62) * mm, v(279.55, 99.18) * mm]});
            skLineSegment(sketch, "E601", {"start": v(289.32, 160.84) * mm, "end": v(280.08, 107.4) * mm});
            skLineSegment(sketch, "E602", {"start": v(280.08, 107.4) * mm, "end": v(289.32, 160.84) * mm});
            skFitSpline(sketch, "E603", {"points": [v(274.67, 98.5) * mm, v(273.07, 98.26) * mm, v(270.89, 97.9) * mm, v(268.12, 97.41) * mm]});
            skFitSpline(sketch, "E604", {"points": [v(268.12, 97.41) * mm, v(267.24, 97.25) * mm, v(266.33, 97.17) * mm, v(265.4, 97.17) * mm]});
            skFitSpline(sketch, "E605", {"points": [v(265.4, 97.17) * mm, v(262.41, 97.17) * mm, v(260.68, 100.17) * mm, v(260.23, 106.14) * mm]});
            skFitSpline(sketch, "E606", {"points": [v(260.23, 106.14) * mm, v(262.03, 105.46) * mm, v(263.47, 105.12) * mm, v(264.56, 105.12) * mm]});
            skFitSpline(sketch, "E607", {"points": [v(264.56, 105.12) * mm, v(267.03, 105.12) * mm, v(269.35, 105.41) * mm, v(271.55, 106) * mm]});
            skLineSegment(sketch, "E608", {"start": v(279.55, 99.18) * mm, "end": v(274.67, 98.5) * mm});
            skLineSegment(sketch, "E609", {"start": v(274.67, 98.5) * mm, "end": v(279.55, 99.18) * mm});
            skFitSpline(sketch, "E610", {"points": [v(279.12, 148.1) * mm, v(275.9, 146) * mm, v(273.11, 144.93) * mm, v(270.76, 144.93) * mm]});
            skFitSpline(sketch, "E611", {"points": [v(270.76, 144.93) * mm, v(266.94, 144.93) * mm, v(265.03, 147.62) * mm, v(265.03, 153.01) * mm]});
            skLineSegment(sketch, "E612", {"start": v(271.55, 106) * mm, "end": v(279.12, 148.1) * mm});
            skLineSegment(sketch, "E613", {"start": v(279.12, 148.1) * mm, "end": v(271.55, 106) * mm});
            skFitSpline(sketch, "E614", {"points": [v(265.03, 154.9) * mm, v(267.08, 153.52) * mm, v(268.93, 152.83) * mm, v(270.57, 152.83) * mm]});
            skFitSpline(sketch, "E615", {"points": [v(270.57, 152.83) * mm, v(273.5, 152.83) * mm, v(278.55, 155.03) * mm, v(285.72, 159.44) * mm]});
            skFitSpline(sketch, "E616", {"points": [v(285.72, 159.44) * mm, v(286.03, 159.62) * mm, v(287.24, 160.1) * mm, v(289.32, 160.84) * mm]});
            skLineSegment(sketch, "E617", {"start": v(265.03, 153.01) * mm, "end": v(265.03, 154.9) * mm});
            skLineSegment(sketch, "E618", {"start": v(265.03, 154.9) * mm, "end": v(265.03, 153.01) * mm});
            skFitSpline(sketch, "E619", {"points": [v(280.08, 107.4) * mm, v(282.1, 107.8) * mm, v(283.8, 107.99) * mm, v(285.15, 107.99) * mm]});
            skFitSpline(sketch, "E620", {"points": [v(285.15, 107.99) * mm, v(288.4, 107.99) * mm, v(290.62, 107.39) * mm, v(291.8, 106.17) * mm]});
            skFitSpline(sketch, "E621", {"points": [v(291.8, 106.17) * mm, v(292.97, 104.96) * mm, v(293.54, 102.4) * mm, v(293.54, 98.48) * mm]});
            skFitSpline(sketch, "E622", {"points": [v(293.54, 98.48) * mm, v(291.66, 99.4) * mm, v(289.75, 99.85) * mm, v(287.82, 99.85) * mm]});
            skFitSpline(sketch, "E623", {"points": [v(287.82, 99.85) * mm, v(285.58, 99.85) * mm, v(282.82, 99.62) * mm, v(279.55, 99.18) * mm]});
            skFitSpline(sketch, "E624", {"points": [v(274.67, 98.5) * mm, v(273.07, 98.26) * mm, v(270.89, 97.9) * mm, v(268.12, 97.41) * mm]});
            skFitSpline(sketch, "E625", {"points": [v(268.12, 97.41) * mm, v(267.24, 97.25) * mm, v(266.33, 97.17) * mm, v(265.4, 97.17) * mm]});
            skFitSpline(sketch, "E626", {"points": [v(265.4, 97.17) * mm, v(262.41, 97.17) * mm, v(260.68, 100.17) * mm, v(260.23, 106.14) * mm]});
            skFitSpline(sketch, "E627", {"points": [v(260.23, 106.14) * mm, v(262.03, 105.46) * mm, v(263.47, 105.12) * mm, v(264.56, 105.12) * mm]});
            skFitSpline(sketch, "E628", {"points": [v(264.56, 105.12) * mm, v(267.03, 105.12) * mm, v(269.35, 105.41) * mm, v(271.55, 106) * mm]});
            skFitSpline(sketch, "E629", {"points": [v(279.12, 148.1) * mm, v(275.9, 146) * mm, v(273.11, 144.93) * mm, v(270.76, 144.93) * mm]});
            skFitSpline(sketch, "E630", {"points": [v(270.76, 144.93) * mm, v(266.94, 144.93) * mm, v(265.03, 147.62) * mm, v(265.03, 153.01) * mm]});
            skFitSpline(sketch, "E631", {"points": [v(265.03, 154.9) * mm, v(267.08, 153.52) * mm, v(268.93, 152.83) * mm, v(270.57, 152.83) * mm]});
            skFitSpline(sketch, "E632", {"points": [v(270.57, 152.83) * mm, v(273.5, 152.83) * mm, v(278.55, 155.03) * mm, v(285.72, 159.44) * mm]});
            skFitSpline(sketch, "E633", {"points": [v(285.72, 159.44) * mm, v(286.03, 159.62) * mm, v(287.24, 160.1) * mm, v(289.32, 160.84) * mm]});
            skFitSpline(sketch, "E634", {"points": [v(335.1, 129.7) * mm, v(334.33, 123.52) * mm, v(332.46, 120.44) * mm, v(329.47, 120.44) * mm]});
            skFitSpline(sketch, "E635", {"points": [v(329.47, 120.44) * mm, v(328.83, 120.44) * mm, v(328.08, 120.5) * mm, v(327.22, 120.6) * mm]});
            skFitSpline(sketch, "E636", {"points": [v(324.46, 120.98) * mm, v(322.76, 121.23) * mm, v(321.44, 121.35) * mm, v(320.51, 121.35) * mm]});
            skFitSpline(sketch, "E637", {"points": [v(320.51, 121.35) * mm, v(319.2, 121.35) * mm, v(317.55, 120.96) * mm, v(315.55, 120.15) * mm]});
            skFitSpline(sketch, "E638", {"points": [v(315.55, 120.15) * mm, v(317, 125.83) * mm, v(319.37, 128.65) * mm, v(322.63, 128.65) * mm]});
            skFitSpline(sketch, "E639", {"points": [v(322.63, 128.65) * mm, v(323.19, 128.65) * mm, v(323.8, 128.6) * mm, v(324.46, 128.53) * mm]});
            skLineSegment(sketch, "E640", {"start": v(327.22, 120.6) * mm, "end": v(324.46, 120.98) * mm});
            skLineSegment(sketch, "E641", {"start": v(324.46, 120.98) * mm, "end": v(327.22, 120.6) * mm});
            skFitSpline(sketch, "E642", {"points": [v(328.31, 128.04) * mm, v(328.94, 127.97) * mm, v(329.62, 127.94) * mm, v(330.34, 127.94) * mm]});
            skFitSpline(sketch, "E643", {"points": [v(330.34, 127.94) * mm, v(331.97, 127.94) * mm, v(333.56, 128.53) * mm, v(335.1, 129.7) * mm]});
            skLineSegment(sketch, "E644", {"start": v(324.46, 128.53) * mm, "end": v(328.31, 128.04) * mm});
            skLineSegment(sketch, "E645", {"start": v(328.31, 128.04) * mm, "end": v(324.46, 128.53) * mm});
            skFitSpline(sketch, "E646", {"points": [v(335.1, 129.7) * mm, v(334.33, 123.52) * mm, v(332.46, 120.44) * mm, v(329.47, 120.44) * mm]});
            skFitSpline(sketch, "E647", {"points": [v(329.47, 120.44) * mm, v(328.83, 120.44) * mm, v(328.08, 120.5) * mm, v(327.22, 120.6) * mm]});
            skFitSpline(sketch, "E648", {"points": [v(324.46, 120.98) * mm, v(322.76, 121.23) * mm, v(321.44, 121.35) * mm, v(320.51, 121.35) * mm]});
            skFitSpline(sketch, "E649", {"points": [v(320.51, 121.35) * mm, v(319.2, 121.35) * mm, v(317.55, 120.96) * mm, v(315.55, 120.15) * mm]});
            skFitSpline(sketch, "E650", {"points": [v(315.55, 120.15) * mm, v(317, 125.83) * mm, v(319.37, 128.65) * mm, v(322.63, 128.65) * mm]});
            skFitSpline(sketch, "E651", {"points": [v(322.63, 128.65) * mm, v(323.19, 128.65) * mm, v(323.8, 128.6) * mm, v(324.46, 128.53) * mm]});
            skFitSpline(sketch, "E652", {"points": [v(328.31, 128.04) * mm, v(328.94, 127.97) * mm, v(329.62, 127.94) * mm, v(330.34, 127.94) * mm]});
            skFitSpline(sketch, "E653", {"points": [v(330.34, 127.94) * mm, v(331.97, 127.94) * mm, v(333.56, 128.53) * mm, v(335.1, 129.7) * mm]});
            skFitSpline(sketch, "E654", {"points": [v(364.48, 107.4) * mm, v(366.5, 107.8) * mm, v(368.19, 107.99) * mm, v(369.54, 107.99) * mm]});
            skFitSpline(sketch, "E655", {"points": [v(369.54, 107.99) * mm, v(372.8, 107.99) * mm, v(375.02, 107.39) * mm, v(376.19, 106.17) * mm]});
            skFitSpline(sketch, "E656", {"points": [v(376.19, 106.17) * mm, v(377.36, 104.96) * mm, v(377.94, 102.4) * mm, v(377.94, 98.48) * mm]});
            skFitSpline(sketch, "E657", {"points": [v(377.94, 98.48) * mm, v(376.06, 99.4) * mm, v(374.15, 99.85) * mm, v(372.22, 99.85) * mm]});
            skFitSpline(sketch, "E658", {"points": [v(372.22, 99.85) * mm, v(369.97, 99.85) * mm, v(367.22, 99.62) * mm, v(363.94, 99.18) * mm]});
            skLineSegment(sketch, "E659", {"start": v(373.71, 160.84) * mm, "end": v(364.48, 107.4) * mm});
            skLineSegment(sketch, "E660", {"start": v(364.48, 107.4) * mm, "end": v(373.71, 160.84) * mm});
            skFitSpline(sketch, "E661", {"points": [v(359.06, 98.5) * mm, v(357.46, 98.26) * mm, v(355.28, 97.9) * mm, v(352.51, 97.41) * mm]});
            skFitSpline(sketch, "E662", {"points": [v(352.51, 97.41) * mm, v(351.63, 97.25) * mm, v(350.72, 97.17) * mm, v(349.78, 97.17) * mm]});
            skFitSpline(sketch, "E663", {"points": [v(349.78, 97.17) * mm, v(346.8, 97.17) * mm, v(345.08, 100.17) * mm, v(344.62, 106.14) * mm]});
            skFitSpline(sketch, "E664", {"points": [v(344.62, 106.14) * mm, v(346.42, 105.46) * mm, v(347.86, 105.12) * mm, v(348.96, 105.12) * mm]});
            skFitSpline(sketch, "E665", {"points": [v(348.96, 105.12) * mm, v(351.42, 105.12) * mm, v(353.75, 105.41) * mm, v(355.95, 106) * mm]});
            skLineSegment(sketch, "E666", {"start": v(363.94, 99.18) * mm, "end": v(359.06, 98.5) * mm});
            skLineSegment(sketch, "E667", {"start": v(359.06, 98.5) * mm, "end": v(363.94, 99.18) * mm});
            skFitSpline(sketch, "E668", {"points": [v(363.52, 148.1) * mm, v(360.3, 146) * mm, v(357.5, 144.93) * mm, v(355.15, 144.93) * mm]});
            skFitSpline(sketch, "E669", {"points": [v(355.15, 144.93) * mm, v(351.33, 144.93) * mm, v(349.42, 147.62) * mm, v(349.42, 153.01) * mm]});
            skLineSegment(sketch, "E670", {"start": v(355.95, 106) * mm, "end": v(363.52, 148.1) * mm});
            skLineSegment(sketch, "E671", {"start": v(363.52, 148.1) * mm, "end": v(355.95, 106) * mm});
            skFitSpline(sketch, "E672", {"points": [v(349.42, 154.9) * mm, v(351.47, 153.52) * mm, v(353.32, 152.83) * mm, v(354.97, 152.83) * mm]});
            skFitSpline(sketch, "E673", {"points": [v(354.97, 152.83) * mm, v(357.89, 152.83) * mm, v(362.94, 155.03) * mm, v(370.12, 159.44) * mm]});
            skFitSpline(sketch, "E674", {"points": [v(370.12, 159.44) * mm, v(370.43, 159.62) * mm, v(371.63, 160.1) * mm, v(373.71, 160.84) * mm]});
            skLineSegment(sketch, "E675", {"start": v(349.42, 153.01) * mm, "end": v(349.42, 154.9) * mm});
            skLineSegment(sketch, "E676", {"start": v(349.42, 154.9) * mm, "end": v(349.42, 153.01) * mm});
            skFitSpline(sketch, "E677", {"points": [v(399.53, 161.29) * mm, v(401.74, 160.06) * mm, v(404.75, 159.45) * mm, v(408.55, 159.45) * mm]});
            skFitSpline(sketch, "E678", {"points": [v(432.57, 150.65) * mm, v(425.06, 143.33) * mm, v(418.97, 135.14) * mm, v(414.28, 126.1) * mm]});
            skFitSpline(sketch, "E679", {"points": [v(414.28, 126.1) * mm, v(409.6, 117.05) * mm, v(407.25, 109.05) * mm, v(407.25, 102.1) * mm]});
            skFitSpline(sketch, "E680", {"points": [v(407.25, 102.1) * mm, v(407.25, 100.52) * mm, v(407.42, 98.58) * mm, v(407.77, 96.28) * mm]});
            skFitSpline(sketch, "E681", {"points": [v(407.77, 96.28) * mm, v(406.64, 95.93) * mm, v(405.75, 95.74) * mm, v(405.08, 95.74) * mm]});
            skFitSpline(sketch, "E682", {"points": [v(405.08, 95.74) * mm, v(400.09, 95.74) * mm, v(397.59, 97.79) * mm, v(397.59, 101.86) * mm]});
            skFitSpline(sketch, "E683", {"points": [v(397.59, 101.86) * mm, v(397.59, 104.73) * mm, v(398.72, 109.17) * mm, v(401, 115.15) * mm]});
            skFitSpline(sketch, "E684", {"points": [v(401, 115.15) * mm, v(403.29, 121.13) * mm, v(405.8, 126.31) * mm, v(408.57, 130.72) * mm]});
            skFitSpline(sketch, "E685", {"points": [v(408.57, 130.72) * mm, v(414.11, 139.56) * mm, v(419.76, 146.08) * mm, v(425.54, 150.28) * mm]});
            skLineSegment(sketch, "E686", {"start": v(408.55, 159.45) * mm, "end": v(410.1, 159.48) * mm});
            skLineSegment(sketch, "E687", {"start": v(410.1, 159.48) * mm, "end": v(414.9, 159.4) * mm});
            skLineSegment(sketch, "E688", {"start": v(414.9, 159.4) * mm, "end": v(419.69, 159.33) * mm});
            skLineSegment(sketch, "E689", {"start": v(419.69, 159.33) * mm, "end": v(433.97, 159.33) * mm});
            skLineSegment(sketch, "E690", {"start": v(433.97, 159.33) * mm, "end": v(432.57, 150.65) * mm});
            skFitSpline(sketch, "E691", {"points": [v(411.55, 150.23) * mm, v(406.34, 150.23) * mm, v(402.84, 150.48) * mm, v(401.06, 150.98) * mm]});
            skFitSpline(sketch, "E692", {"points": [v(401.06, 150.98) * mm, v(399.28, 151.48) * mm, v(398.39, 152.65) * mm, v(398.39, 154.51) * mm]});
            skFitSpline(sketch, "E693", {"points": [v(398.39, 154.51) * mm, v(398.39, 155.11) * mm, v(398.47, 155.9) * mm, v(398.64, 156.83) * mm]});
            skFitSpline(sketch, "E694", {"points": [v(398.64, 156.83) * mm, v(398.73, 157.24) * mm, v(398.84, 157.8) * mm, v(398.98, 158.52) * mm]});
            skLineSegment(sketch, "E695", {"start": v(425.54, 150.28) * mm, "end": v(413.55, 150.28) * mm});
            skLineSegment(sketch, "E696", {"start": v(413.55, 150.28) * mm, "end": v(411.55, 150.23) * mm});
            skLineSegment(sketch, "E697", {"start": v(411.55, 150.23) * mm, "end": v(425.54, 150.28) * mm});
            skLineSegment(sketch, "E698", {"start": v(398.98, 158.52) * mm, "end": v(399.53, 161.29) * mm});
            skLineSegment(sketch, "E699", {"start": v(399.53, 161.29) * mm, "end": v(398.98, 158.52) * mm});
            skFitSpline(sketch, "E700", {"points": [v(364.48, 107.4) * mm, v(366.5, 107.8) * mm, v(368.19, 107.99) * mm, v(369.54, 107.99) * mm]});
            skFitSpline(sketch, "E701", {"points": [v(369.54, 107.99) * mm, v(372.8, 107.99) * mm, v(375.02, 107.39) * mm, v(376.19, 106.17) * mm]});
            skFitSpline(sketch, "E702", {"points": [v(376.19, 106.17) * mm, v(377.36, 104.96) * mm, v(377.94, 102.4) * mm, v(377.94, 98.48) * mm]});
            skFitSpline(sketch, "E703", {"points": [v(377.94, 98.48) * mm, v(376.06, 99.4) * mm, v(374.15, 99.85) * mm, v(372.22, 99.85) * mm]});
            skFitSpline(sketch, "E704", {"points": [v(372.22, 99.85) * mm, v(369.97, 99.85) * mm, v(367.22, 99.62) * mm, v(363.94, 99.18) * mm]});
            skFitSpline(sketch, "E705", {"points": [v(359.06, 98.5) * mm, v(357.46, 98.26) * mm, v(355.28, 97.9) * mm, v(352.51, 97.41) * mm]});
            skFitSpline(sketch, "E706", {"points": [v(352.51, 97.41) * mm, v(351.63, 97.25) * mm, v(350.72, 97.17) * mm, v(349.78, 97.17) * mm]});
            skFitSpline(sketch, "E707", {"points": [v(349.78, 97.17) * mm, v(346.8, 97.17) * mm, v(345.08, 100.17) * mm, v(344.62, 106.14) * mm]});
            skFitSpline(sketch, "E708", {"points": [v(344.62, 106.14) * mm, v(346.42, 105.46) * mm, v(347.86, 105.12) * mm, v(348.96, 105.12) * mm]});
            skFitSpline(sketch, "E709", {"points": [v(348.96, 105.12) * mm, v(351.42, 105.12) * mm, v(353.75, 105.41) * mm, v(355.95, 106) * mm]});
            skFitSpline(sketch, "E710", {"points": [v(363.52, 148.1) * mm, v(360.3, 146) * mm, v(357.5, 144.93) * mm, v(355.15, 144.93) * mm]});
            skFitSpline(sketch, "E711", {"points": [v(355.15, 144.93) * mm, v(351.33, 144.93) * mm, v(349.42, 147.62) * mm, v(349.42, 153.01) * mm]});
            skFitSpline(sketch, "E712", {"points": [v(349.42, 154.9) * mm, v(351.47, 153.52) * mm, v(353.32, 152.83) * mm, v(354.97, 152.83) * mm]});
            skFitSpline(sketch, "E713", {"points": [v(354.97, 152.83) * mm, v(357.89, 152.83) * mm, v(362.94, 155.03) * mm, v(370.12, 159.44) * mm]});
            skFitSpline(sketch, "E714", {"points": [v(370.12, 159.44) * mm, v(370.43, 159.62) * mm, v(371.63, 160.1) * mm, v(373.71, 160.84) * mm]});
            skFitSpline(sketch, "E715", {"points": [v(399.53, 161.29) * mm, v(401.74, 160.06) * mm, v(404.75, 159.45) * mm, v(408.55, 159.45) * mm]});
            skFitSpline(sketch, "E716", {"points": [v(432.57, 150.65) * mm, v(425.06, 143.33) * mm, v(418.97, 135.14) * mm, v(414.28, 126.1) * mm]});
            skFitSpline(sketch, "E717", {"points": [v(414.28, 126.1) * mm, v(409.6, 117.05) * mm, v(407.25, 109.05) * mm, v(407.25, 102.1) * mm]});
            skFitSpline(sketch, "E718", {"points": [v(407.25, 102.1) * mm, v(407.25, 100.52) * mm, v(407.42, 98.58) * mm, v(407.77, 96.28) * mm]});
            skFitSpline(sketch, "E719", {"points": [v(407.77, 96.28) * mm, v(406.64, 95.93) * mm, v(405.75, 95.74) * mm, v(405.08, 95.74) * mm]});
            skFitSpline(sketch, "E720", {"points": [v(405.08, 95.74) * mm, v(400.09, 95.74) * mm, v(397.59, 97.79) * mm, v(397.59, 101.86) * mm]});
            skFitSpline(sketch, "E721", {"points": [v(397.59, 101.86) * mm, v(397.59, 104.73) * mm, v(398.72, 109.17) * mm, v(401, 115.15) * mm]});
            skFitSpline(sketch, "E722", {"points": [v(401, 115.15) * mm, v(403.29, 121.13) * mm, v(405.8, 126.31) * mm, v(408.57, 130.72) * mm]});
            skFitSpline(sketch, "E723", {"points": [v(408.57, 130.72) * mm, v(414.11, 139.56) * mm, v(419.76, 146.08) * mm, v(425.54, 150.28) * mm]});
            skFitSpline(sketch, "E724", {"points": [v(411.55, 150.23) * mm, v(406.34, 150.23) * mm, v(402.84, 150.48) * mm, v(401.06, 150.98) * mm]});
            skFitSpline(sketch, "E725", {"points": [v(401.06, 150.98) * mm, v(399.28, 151.48) * mm, v(398.39, 152.65) * mm, v(398.39, 154.51) * mm]});
            skFitSpline(sketch, "E726", {"points": [v(398.39, 154.51) * mm, v(398.39, 155.11) * mm, v(398.47, 155.9) * mm, v(398.64, 156.83) * mm]});
            skFitSpline(sketch, "E727", {"points": [v(398.64, 156.83) * mm, v(398.73, 157.24) * mm, v(398.84, 157.8) * mm, v(398.98, 158.52) * mm]});
            skLineSegment(sketch, "E728", {"start": v(279.4, 609.6) * mm, "end": v(278.58, 0) * mm, "construction": true});
            skArc(sketch, "E729.filletArc", {"start": v(287.95, 342.07) * mm, "mid": v(287.71, 342.53) * mm, "end": v(287.21, 342.41) * mm});
            skSolve(sketch);
        }
        {
            var Q0;
            Q0 = qSketchRegion(id + "F2", true);
            extrude(context, id + "F3", {"entities" : qUnion([Q0]), "operationType" : NewBodyOperationType.REMOVE, "oppositeDirection" : true, "depth" : 4.76 * mm});
        }
        {
            var Q0;
            {var subQ0=sQuery(id+"F0.wireOp",EDGE,"E4.filletArc");var subQ1=sQuery(id+"F0.wireOp",EDGE,"E3.filletArc");var subQ2=sQuery(id+"F0.wireOp",EDGE,"E2.filletArc");var subQ3=sQuery(id+"F0.wireOp",EDGE,"E1.filletArc");var subQ4=sQuery(id+"F0.wireOp",EDGE,"E0.bottom");var subQ5=sQuery(id+"F0.wireOp",EDGE,"E0.right");var subQ6=sQuery(id+"F0.wireOp",EDGE,"E0.top");var subQ7=sQuery(id+"F0.wireOp",EDGE,"E0.left");Q0=makeQuery(id+"F3.boolean.opBoolean","SPLIT",FACE,{"disambiguationData":[TD([makeQuery(id+"F1.opExtrude","SWEPT_FACE",FACE,{"disambiguationData":[OSD([subQ4])]})])],"derivedFrom":makeQuery(id+"F1.opExtrude","CAP_FACE",FACE,{"disambiguationData":[OSD([subQ4,subQ6,subQ7,subQ5,subQ3,subQ2,subQ1,subQ0])],"isStart":false})});}
            var sketch = newSketch(context, id + "F4", { "sketchPlane" : qUnion([Q0])});
            skLineSegment(sketch, "E730.bottom", {"start": v(0, 417.64) * mm, "end": v(558.8, 417.64) * mm});
            skLineSegment(sketch, "E730.top", {"start": v(0, 306.52) * mm, "end": v(558.8, 306.52) * mm});
            skLineSegment(sketch, "E731.0", {"start": v(0, 12.7) * mm, "end": v(0, 306.52) * mm});
            skArc(sketch, "E732.0", {"start": v(0, 12.7) * mm, "mid": v(3.72, 3.72) * mm, "end": v(12.7, 0) * mm});
            skLineSegment(sketch, "E733.0", {"start": v(12.7, 0) * mm, "end": v(546.1, 0) * mm});
            skArc(sketch, "E734.0", {"start": v(546.1, 0) * mm, "mid": v(555.08, 3.72) * mm, "end": v(558.8, 12.7) * mm});
            skLineSegment(sketch, "E734.1", {"start": v(558.8, 12.7) * mm, "end": v(558.8, 306.52) * mm});
            skLineSegment(sketch, "E735.trimOffspring", {"start": v(0, 417.64) * mm, "end": v(0, 596.9) * mm});
            skLineSegment(sketch, "E736.trimOffspring", {"start": v(558.8, 417.64) * mm, "end": v(558.8, 596.9) * mm});
            skArc(sketch, "E737.0", {"start": v(12.7, 609.6) * mm, "mid": v(3.72, 605.88) * mm, "end": v(0, 596.9) * mm});
            skLineSegment(sketch, "E737.1", {"start": v(12.7, 609.6) * mm, "end": v(546.1, 609.6) * mm});
            skArc(sketch, "E738.0", {"start": v(558.8, 596.9) * mm, "mid": v(555.08, 605.88) * mm, "end": v(546.1, 609.6) * mm});
            skSolve(sketch);
        }
        {
            var Q0;
            Q0 = qSketchRegion(id + "F4", true);
            extrude(context, id + "F5", {"entities" : qUnion([Q0]), "operationType" : NewBodyOperationType.REMOVE, "endBound" : BoundingType.THROUGH_ALL, "oppositeDirection" : true, "depth" : 25.4 * mm});
        }
    });
